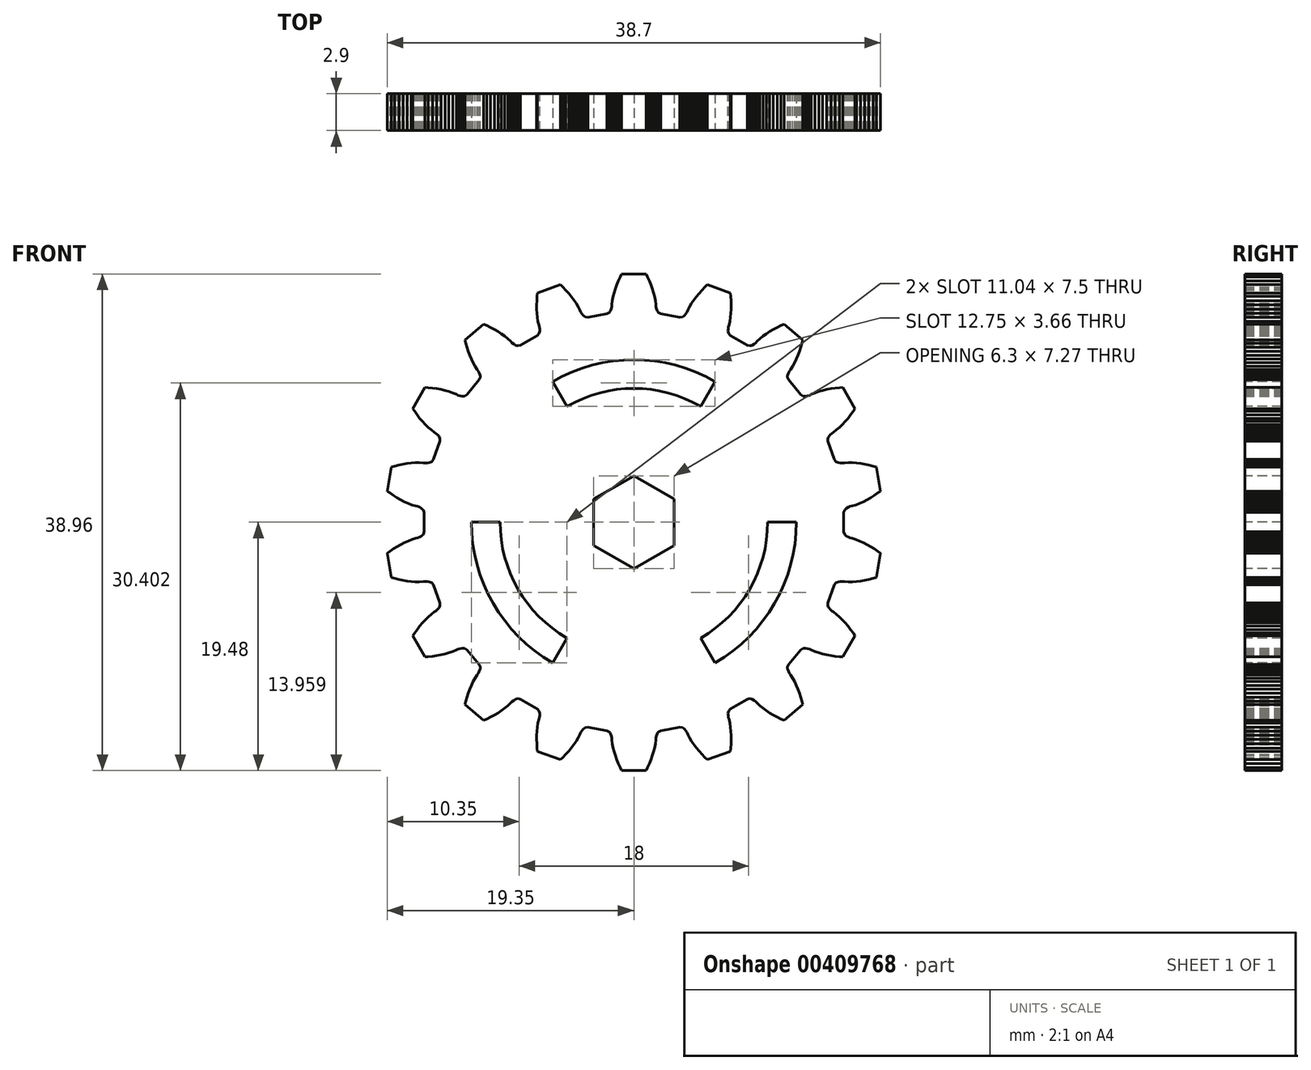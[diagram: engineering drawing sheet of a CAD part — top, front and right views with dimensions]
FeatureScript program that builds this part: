
annotation { "Feature Type Name" : "Feature", "Feature Type Description" : "" }
export const myFeature = defineFeature(function(context is Context, id is Id, definition is map)
    precondition{}
    {
        {
            var Q0;
            Q0=qCreatedBy(makeId("Front.planeOp"),FACE);
            var sketch = newSketch(context, id + "F0", { "sketchPlane" : qUnion([Q0])});
            skLineSegment(sketch, "E0", {"start": v(-16.48, 0.76) * mm, "end": v(-16.54, 0.96) * mm});
            skLineSegment(sketch, "E1", {"start": v(-16.54, 0.96) * mm, "end": v(-16.61, 1.04) * mm});
            skLineSegment(sketch, "E2", {"start": v(-16.61, 1.04) * mm, "end": v(-16.68, 1.1) * mm});
            skLineSegment(sketch, "E3", {"start": v(-16.68, 1.1) * mm, "end": v(-16.83, 1.17) * mm});
            skLineSegment(sketch, "E4", {"start": v(-16.83, 1.17) * mm, "end": v(-16.98, 1.24) * mm});
            skLineSegment(sketch, "E5", {"start": v(-16.98, 1.24) * mm, "end": v(-17.12, 1.27) * mm});
            skLineSegment(sketch, "E6", {"start": v(-17.12, 1.27) * mm, "end": v(-17.42, 1.36) * mm});
            skLineSegment(sketch, "E7", {"start": v(-17.42, 1.36) * mm, "end": v(-17.71, 1.47) * mm});
            skLineSegment(sketch, "E8", {"start": v(-17.71, 1.47) * mm, "end": v(-18, 1.6) * mm});
            skLineSegment(sketch, "E9", {"start": v(-18, 1.6) * mm, "end": v(-18.3, 1.75) * mm});
            skLineSegment(sketch, "E10", {"start": v(-18.3, 1.75) * mm, "end": v(-18.58, 1.92) * mm});
            skLineSegment(sketch, "E11", {"start": v(-18.58, 1.92) * mm, "end": v(-18.86, 2.1) * mm});
            skLineSegment(sketch, "E12", {"start": v(-18.86, 2.1) * mm, "end": v(-19.15, 2.29) * mm});
            skLineSegment(sketch, "E13", {"start": v(-19.15, 2.29) * mm, "end": v(-19.35, 2.44) * mm});
            skLineSegment(sketch, "E14", {"start": v(-19.35, 2.44) * mm, "end": v(-19.02, 4.33) * mm});
            skLineSegment(sketch, "E15", {"start": v(-19.02, 4.33) * mm, "end": v(-18.77, 4.4) * mm});
            skLineSegment(sketch, "E16", {"start": v(-18.77, 4.4) * mm, "end": v(-18.44, 4.48) * mm});
            skLineSegment(sketch, "E17", {"start": v(-18.44, 4.48) * mm, "end": v(-18.11, 4.56) * mm});
            skLineSegment(sketch, "E18", {"start": v(-18.11, 4.56) * mm, "end": v(-17.79, 4.61) * mm});
            skLineSegment(sketch, "E19", {"start": v(-17.79, 4.61) * mm, "end": v(-17.47, 4.65) * mm});
            skLineSegment(sketch, "E20", {"start": v(-17.47, 4.65) * mm, "end": v(-17.15, 4.67) * mm});
            skLineSegment(sketch, "E21", {"start": v(-17.15, 4.67) * mm, "end": v(-16.83, 4.68) * mm});
            skLineSegment(sketch, "E22", {"start": v(-16.83, 4.68) * mm, "end": v(-16.53, 4.66) * mm});
            skLineSegment(sketch, "E23", {"start": v(-16.53, 4.66) * mm, "end": v(-16.37, 4.64) * mm});
            skLineSegment(sketch, "E24", {"start": v(-16.37, 4.64) * mm, "end": v(-16.22, 4.65) * mm});
            skLineSegment(sketch, "E25", {"start": v(-16.22, 4.65) * mm, "end": v(-16.05, 4.68) * mm});
            skLineSegment(sketch, "E26", {"start": v(-16.05, 4.68) * mm, "end": v(-15.96, 4.7) * mm});
            skLineSegment(sketch, "E27", {"start": v(-15.96, 4.7) * mm, "end": v(-15.87, 4.76) * mm});
            skLineSegment(sketch, "E28", {"start": v(-15.87, 4.76) * mm, "end": v(-15.74, 4.92) * mm});
            skLineSegment(sketch, "E29", {"start": v(-15.74, 4.92) * mm, "end": v(-15.22, 6.35) * mm});
            skLineSegment(sketch, "E30", {"start": v(-15.22, 6.35) * mm, "end": v(-15.22, 6.56) * mm});
            skLineSegment(sketch, "E31", {"start": v(-15.22, 6.56) * mm, "end": v(-15.26, 6.65) * mm});
            skLineSegment(sketch, "E32", {"start": v(-15.26, 6.65) * mm, "end": v(-15.3, 6.73) * mm});
            skLineSegment(sketch, "E33", {"start": v(-15.3, 6.73) * mm, "end": v(-15.41, 6.86) * mm});
            skLineSegment(sketch, "E34", {"start": v(-15.41, 6.86) * mm, "end": v(-15.53, 6.97) * mm});
            skLineSegment(sketch, "E35", {"start": v(-15.53, 6.97) * mm, "end": v(-15.66, 7.05) * mm});
            skLineSegment(sketch, "E36", {"start": v(-15.66, 7.05) * mm, "end": v(-15.9, 7.24) * mm});
            skLineSegment(sketch, "E37", {"start": v(-15.9, 7.24) * mm, "end": v(-16.14, 7.44) * mm});
            skLineSegment(sketch, "E38", {"start": v(-16.14, 7.44) * mm, "end": v(-16.37, 7.66) * mm});
            skLineSegment(sketch, "E39", {"start": v(-16.37, 7.66) * mm, "end": v(-16.6, 7.9) * mm});
            skLineSegment(sketch, "E40", {"start": v(-16.6, 7.9) * mm, "end": v(-16.8, 8.15) * mm});
            skLineSegment(sketch, "E41", {"start": v(-16.8, 8.15) * mm, "end": v(-17.01, 8.42) * mm});
            skLineSegment(sketch, "E42", {"start": v(-17.01, 8.42) * mm, "end": v(-17.2, 8.7) * mm});
            skLineSegment(sketch, "E43", {"start": v(-17.2, 8.7) * mm, "end": v(-17.35, 8.91) * mm});
            skLineSegment(sketch, "E44", {"start": v(-17.35, 8.91) * mm, "end": v(-16.4, 10.57) * mm});
            skLineSegment(sketch, "E45", {"start": v(-16.4, 10.57) * mm, "end": v(-16.14, 10.55) * mm});
            skLineSegment(sketch, "E46", {"start": v(-16.14, 10.55) * mm, "end": v(-15.8, 10.52) * mm});
            skLineSegment(sketch, "E47", {"start": v(-15.8, 10.52) * mm, "end": v(-15.46, 10.48) * mm});
            skLineSegment(sketch, "E48", {"start": v(-15.46, 10.48) * mm, "end": v(-15.14, 10.42) * mm});
            skLineSegment(sketch, "E49", {"start": v(-15.14, 10.42) * mm, "end": v(-14.82, 10.34) * mm});
            skLineSegment(sketch, "E50", {"start": v(-14.82, 10.34) * mm, "end": v(-14.52, 10.26) * mm});
            skLineSegment(sketch, "E51", {"start": v(-14.52, 10.26) * mm, "end": v(-14.22, 10.16) * mm});
            skLineSegment(sketch, "E52", {"start": v(-14.22, 10.16) * mm, "end": v(-13.93, 10.03) * mm});
            skLineSegment(sketch, "E53", {"start": v(-13.93, 10.03) * mm, "end": v(-13.8, 9.96) * mm});
            skLineSegment(sketch, "E54", {"start": v(-13.8, 9.96) * mm, "end": v(-13.65, 9.92) * mm});
            skLineSegment(sketch, "E55", {"start": v(-13.65, 9.92) * mm, "end": v(-13.48, 9.89) * mm});
            skLineSegment(sketch, "E56", {"start": v(-13.48, 9.89) * mm, "end": v(-13.4, 9.88) * mm});
            skLineSegment(sketch, "E57", {"start": v(-13.4, 9.88) * mm, "end": v(-13.29, 9.9) * mm});
            skLineSegment(sketch, "E58", {"start": v(-13.29, 9.9) * mm, "end": v(-13.11, 10) * mm});
            skLineSegment(sketch, "E59", {"start": v(-13.11, 10) * mm, "end": v(-12.13, 11.17) * mm});
            skLineSegment(sketch, "E60", {"start": v(-12.13, 11.17) * mm, "end": v(-12.05, 11.37) * mm});
            skLineSegment(sketch, "E61", {"start": v(-12.05, 11.37) * mm, "end": v(-12.06, 11.47) * mm});
            skLineSegment(sketch, "E62", {"start": v(-12.06, 11.47) * mm, "end": v(-12.08, 11.56) * mm});
            skLineSegment(sketch, "E63", {"start": v(-12.08, 11.56) * mm, "end": v(-12.14, 11.72) * mm});
            skLineSegment(sketch, "E64", {"start": v(-12.14, 11.72) * mm, "end": v(-12.2, 11.86) * mm});
            skLineSegment(sketch, "E65", {"start": v(-12.2, 11.86) * mm, "end": v(-12.3, 11.98) * mm});
            skLineSegment(sketch, "E66", {"start": v(-12.3, 11.98) * mm, "end": v(-12.47, 12.24) * mm});
            skLineSegment(sketch, "E67", {"start": v(-12.47, 12.24) * mm, "end": v(-12.62, 12.51) * mm});
            skLineSegment(sketch, "E68", {"start": v(-12.62, 12.51) * mm, "end": v(-12.76, 12.8) * mm});
            skLineSegment(sketch, "E69", {"start": v(-12.76, 12.8) * mm, "end": v(-12.89, 13.1) * mm});
            skLineSegment(sketch, "E70", {"start": v(-12.89, 13.1) * mm, "end": v(-13, 13.41) * mm});
            skLineSegment(sketch, "E71", {"start": v(-13, 13.41) * mm, "end": v(-13.1, 13.73) * mm});
            skLineSegment(sketch, "E72", {"start": v(-13.1, 13.73) * mm, "end": v(-13.2, 14.06) * mm});
            skLineSegment(sketch, "E73", {"start": v(-13.2, 14.06) * mm, "end": v(-13.26, 14.3) * mm});
            skLineSegment(sketch, "E74", {"start": v(-13.26, 14.3) * mm, "end": v(-11.8, 15.54) * mm});
            skLineSegment(sketch, "E75", {"start": v(-11.8, 15.54) * mm, "end": v(-11.55, 15.44) * mm});
            skLineSegment(sketch, "E76", {"start": v(-11.55, 15.44) * mm, "end": v(-11.25, 15.29) * mm});
            skLineSegment(sketch, "E77", {"start": v(-11.25, 15.29) * mm, "end": v(-10.95, 15.13) * mm});
            skLineSegment(sketch, "E78", {"start": v(-10.95, 15.13) * mm, "end": v(-10.66, 14.97) * mm});
            skLineSegment(sketch, "E79", {"start": v(-10.66, 14.97) * mm, "end": v(-10.4, 14.8) * mm});
            skLineSegment(sketch, "E80", {"start": v(-10.4, 14.8) * mm, "end": v(-10.13, 14.6) * mm});
            skLineSegment(sketch, "E81", {"start": v(-10.13, 14.6) * mm, "end": v(-9.89, 14.4) * mm});
            skLineSegment(sketch, "E82", {"start": v(-9.89, 14.4) * mm, "end": v(-9.66, 14.2) * mm});
            skLineSegment(sketch, "E83", {"start": v(-9.66, 14.2) * mm, "end": v(-9.56, 14.08) * mm});
            skLineSegment(sketch, "E84", {"start": v(-9.56, 14.08) * mm, "end": v(-9.43, 13.99) * mm});
            skLineSegment(sketch, "E85", {"start": v(-9.43, 13.99) * mm, "end": v(-9.29, 13.9) * mm});
            skLineSegment(sketch, "E86", {"start": v(-9.29, 13.9) * mm, "end": v(-9.2, 13.87) * mm});
            skLineSegment(sketch, "E87", {"start": v(-9.2, 13.87) * mm, "end": v(-9.1, 13.85) * mm});
            skLineSegment(sketch, "E88", {"start": v(-9.1, 13.85) * mm, "end": v(-8.9, 13.89) * mm});
            skLineSegment(sketch, "E89", {"start": v(-8.9, 13.89) * mm, "end": v(-7.58, 14.65) * mm});
            skLineSegment(sketch, "E90", {"start": v(-7.58, 14.65) * mm, "end": v(-7.44, 14.8) * mm});
            skLineSegment(sketch, "E91", {"start": v(-7.44, 14.8) * mm, "end": v(-7.4, 14.9) * mm});
            skLineSegment(sketch, "E92", {"start": v(-7.4, 14.9) * mm, "end": v(-7.4, 15) * mm});
            skLineSegment(sketch, "E93", {"start": v(-7.4, 15) * mm, "end": v(-7.4, 15.16) * mm});
            skLineSegment(sketch, "E94", {"start": v(-7.4, 15.16) * mm, "end": v(-7.42, 15.32) * mm});
            skLineSegment(sketch, "E95", {"start": v(-7.42, 15.32) * mm, "end": v(-7.46, 15.47) * mm});
            skLineSegment(sketch, "E96", {"start": v(-7.46, 15.47) * mm, "end": v(-7.53, 15.77) * mm});
            skLineSegment(sketch, "E97", {"start": v(-7.53, 15.77) * mm, "end": v(-7.58, 16.08) * mm});
            skLineSegment(sketch, "E98", {"start": v(-7.58, 16.08) * mm, "end": v(-7.61, 16.4) * mm});
            skLineSegment(sketch, "E99", {"start": v(-7.61, 16.4) * mm, "end": v(-7.63, 16.72) * mm});
            skLineSegment(sketch, "E100", {"start": v(-7.63, 16.72) * mm, "end": v(-7.63, 17.05) * mm});
            skLineSegment(sketch, "E101", {"start": v(-7.63, 17.05) * mm, "end": v(-7.62, 17.38) * mm});
            skLineSegment(sketch, "E102", {"start": v(-7.62, 17.38) * mm, "end": v(-7.6, 17.72) * mm});
            skLineSegment(sketch, "E103", {"start": v(-7.6, 17.72) * mm, "end": v(-7.56, 17.98) * mm});
            skLineSegment(sketch, "E104", {"start": v(-7.56, 17.98) * mm, "end": v(-5.76, 18.64) * mm});
            skLineSegment(sketch, "E105", {"start": v(-5.76, 18.64) * mm, "end": v(-5.58, 18.46) * mm});
            skLineSegment(sketch, "E106", {"start": v(-5.58, 18.46) * mm, "end": v(-5.34, 18.21) * mm});
            skLineSegment(sketch, "E107", {"start": v(-5.34, 18.21) * mm, "end": v(-5.11, 17.97) * mm});
            skLineSegment(sketch, "E108", {"start": v(-5.11, 17.97) * mm, "end": v(-4.9, 17.71) * mm});
            skLineSegment(sketch, "E109", {"start": v(-4.9, 17.71) * mm, "end": v(-4.7, 17.45) * mm});
            skLineSegment(sketch, "E110", {"start": v(-4.7, 17.45) * mm, "end": v(-4.53, 17.19) * mm});
            skLineSegment(sketch, "E111", {"start": v(-4.53, 17.19) * mm, "end": v(-4.36, 16.92) * mm});
            skLineSegment(sketch, "E112", {"start": v(-4.36, 16.92) * mm, "end": v(-4.23, 16.64) * mm});
            skLineSegment(sketch, "E113", {"start": v(-4.23, 16.64) * mm, "end": v(-4.17, 16.5) * mm});
            skLineSegment(sketch, "E114", {"start": v(-4.17, 16.5) * mm, "end": v(-4.08, 16.37) * mm});
            skLineSegment(sketch, "E115", {"start": v(-4.08, 16.37) * mm, "end": v(-3.97, 16.24) * mm});
            skLineSegment(sketch, "E116", {"start": v(-3.97, 16.24) * mm, "end": v(-3.9, 16.18) * mm});
            skLineSegment(sketch, "E117", {"start": v(-3.9, 16.18) * mm, "end": v(-3.82, 16.12) * mm});
            skLineSegment(sketch, "E118", {"start": v(-3.82, 16.12) * mm, "end": v(-3.61, 16.1) * mm});
            skLineSegment(sketch, "E119", {"start": v(-3.61, 16.1) * mm, "end": v(-2.11, 16.36) * mm});
            skLineSegment(sketch, "E120", {"start": v(-2.11, 16.36) * mm, "end": v(-1.93, 16.46) * mm});
            skLineSegment(sketch, "E121", {"start": v(-1.93, 16.46) * mm, "end": v(-1.86, 16.54) * mm});
            skLineSegment(sketch, "E122", {"start": v(-1.86, 16.54) * mm, "end": v(-1.82, 16.62) * mm});
            skLineSegment(sketch, "E123", {"start": v(-1.82, 16.62) * mm, "end": v(-1.77, 16.78) * mm});
            skLineSegment(sketch, "E124", {"start": v(-1.77, 16.78) * mm, "end": v(-1.73, 16.93) * mm});
            skLineSegment(sketch, "E125", {"start": v(-1.73, 16.93) * mm, "end": v(-1.72, 17.08) * mm});
            skLineSegment(sketch, "E126", {"start": v(-1.72, 17.08) * mm, "end": v(-1.69, 17.4) * mm});
            skLineSegment(sketch, "E127", {"start": v(-1.69, 17.4) * mm, "end": v(-1.63, 17.7) * mm});
            skLineSegment(sketch, "E128", {"start": v(-1.63, 17.7) * mm, "end": v(-1.55, 18) * mm});
            skLineSegment(sketch, "E129", {"start": v(-1.55, 18) * mm, "end": v(-1.45, 18.32) * mm});
            skLineSegment(sketch, "E130", {"start": v(-1.45, 18.32) * mm, "end": v(-1.34, 18.63) * mm});
            skLineSegment(sketch, "E131", {"start": v(-1.34, 18.63) * mm, "end": v(-1.21, 18.94) * mm});
            skLineSegment(sketch, "E132", {"start": v(-1.21, 18.94) * mm, "end": v(-1.07, 19.25) * mm});
            skLineSegment(sketch, "E133", {"start": v(-1.07, 19.25) * mm, "end": v(-0.96, 19.48) * mm});
            skLineSegment(sketch, "E134", {"start": v(-0.96, 19.48) * mm, "end": v(0.96, 19.48) * mm});
            skLineSegment(sketch, "E135", {"start": v(0.96, 19.48) * mm, "end": v(1.07, 19.25) * mm});
            skLineSegment(sketch, "E136", {"start": v(1.07, 19.25) * mm, "end": v(1.21, 18.94) * mm});
            skLineSegment(sketch, "E137", {"start": v(1.21, 18.94) * mm, "end": v(1.34, 18.63) * mm});
            skLineSegment(sketch, "E138", {"start": v(1.34, 18.63) * mm, "end": v(1.45, 18.32) * mm});
            skLineSegment(sketch, "E139", {"start": v(1.45, 18.32) * mm, "end": v(1.55, 18) * mm});
            skLineSegment(sketch, "E140", {"start": v(1.55, 18) * mm, "end": v(1.63, 17.7) * mm});
            skLineSegment(sketch, "E141", {"start": v(1.63, 17.7) * mm, "end": v(1.69, 17.4) * mm});
            skLineSegment(sketch, "E142", {"start": v(1.69, 17.4) * mm, "end": v(1.72, 17.08) * mm});
            skLineSegment(sketch, "E143", {"start": v(1.72, 17.08) * mm, "end": v(1.73, 16.93) * mm});
            skLineSegment(sketch, "E144", {"start": v(1.73, 16.93) * mm, "end": v(1.77, 16.78) * mm});
            skLineSegment(sketch, "E145", {"start": v(1.77, 16.78) * mm, "end": v(1.82, 16.62) * mm});
            skLineSegment(sketch, "E146", {"start": v(1.82, 16.62) * mm, "end": v(1.86, 16.54) * mm});
            skLineSegment(sketch, "E147", {"start": v(1.86, 16.54) * mm, "end": v(1.93, 16.46) * mm});
            skLineSegment(sketch, "E148", {"start": v(1.93, 16.46) * mm, "end": v(2.11, 16.36) * mm});
            skLineSegment(sketch, "E149", {"start": v(2.11, 16.36) * mm, "end": v(3.61, 16.1) * mm});
            skLineSegment(sketch, "E150", {"start": v(3.61, 16.1) * mm, "end": v(3.82, 16.12) * mm});
            skLineSegment(sketch, "E151", {"start": v(3.82, 16.12) * mm, "end": v(3.9, 16.18) * mm});
            skLineSegment(sketch, "E152", {"start": v(3.9, 16.18) * mm, "end": v(3.97, 16.24) * mm});
            skLineSegment(sketch, "E153", {"start": v(3.97, 16.24) * mm, "end": v(4.08, 16.37) * mm});
            skLineSegment(sketch, "E154", {"start": v(4.08, 16.37) * mm, "end": v(4.17, 16.5) * mm});
            skLineSegment(sketch, "E155", {"start": v(4.17, 16.5) * mm, "end": v(4.23, 16.64) * mm});
            skLineSegment(sketch, "E156", {"start": v(4.23, 16.64) * mm, "end": v(4.36, 16.92) * mm});
            skLineSegment(sketch, "E157", {"start": v(4.36, 16.92) * mm, "end": v(4.53, 17.19) * mm});
            skLineSegment(sketch, "E158", {"start": v(4.53, 17.19) * mm, "end": v(4.7, 17.45) * mm});
            skLineSegment(sketch, "E159", {"start": v(4.7, 17.45) * mm, "end": v(4.9, 17.71) * mm});
            skLineSegment(sketch, "E160", {"start": v(4.9, 17.71) * mm, "end": v(5.11, 17.97) * mm});
            skLineSegment(sketch, "E161", {"start": v(5.11, 17.97) * mm, "end": v(5.34, 18.21) * mm});
            skLineSegment(sketch, "E162", {"start": v(5.34, 18.21) * mm, "end": v(5.58, 18.46) * mm});
            skLineSegment(sketch, "E163", {"start": v(5.58, 18.46) * mm, "end": v(5.76, 18.64) * mm});
            skLineSegment(sketch, "E164", {"start": v(5.76, 18.64) * mm, "end": v(7.56, 17.98) * mm});
            skLineSegment(sketch, "E165", {"start": v(7.56, 17.98) * mm, "end": v(7.6, 17.72) * mm});
            skLineSegment(sketch, "E166", {"start": v(7.6, 17.72) * mm, "end": v(7.62, 17.38) * mm});
            skLineSegment(sketch, "E167", {"start": v(7.62, 17.38) * mm, "end": v(7.63, 17.05) * mm});
            skLineSegment(sketch, "E168", {"start": v(7.63, 17.05) * mm, "end": v(7.63, 16.72) * mm});
            skLineSegment(sketch, "E169", {"start": v(7.63, 16.72) * mm, "end": v(7.61, 16.4) * mm});
            skLineSegment(sketch, "E170", {"start": v(7.61, 16.4) * mm, "end": v(7.58, 16.08) * mm});
            skLineSegment(sketch, "E171", {"start": v(7.58, 16.08) * mm, "end": v(7.53, 15.77) * mm});
            skLineSegment(sketch, "E172", {"start": v(7.53, 15.77) * mm, "end": v(7.46, 15.47) * mm});
            skLineSegment(sketch, "E173", {"start": v(7.46, 15.47) * mm, "end": v(7.42, 15.32) * mm});
            skLineSegment(sketch, "E174", {"start": v(7.42, 15.32) * mm, "end": v(7.4, 15.16) * mm});
            skLineSegment(sketch, "E175", {"start": v(7.4, 15.16) * mm, "end": v(7.4, 15) * mm});
            skLineSegment(sketch, "E176", {"start": v(7.4, 15) * mm, "end": v(7.4, 14.9) * mm});
            skLineSegment(sketch, "E177", {"start": v(7.4, 14.9) * mm, "end": v(7.44, 14.8) * mm});
            skLineSegment(sketch, "E178", {"start": v(7.44, 14.8) * mm, "end": v(7.58, 14.65) * mm});
            skLineSegment(sketch, "E179", {"start": v(7.58, 14.65) * mm, "end": v(8.9, 13.89) * mm});
            skLineSegment(sketch, "E180", {"start": v(8.9, 13.89) * mm, "end": v(9.1, 13.85) * mm});
            skLineSegment(sketch, "E181", {"start": v(9.1, 13.85) * mm, "end": v(9.2, 13.87) * mm});
            skLineSegment(sketch, "E182", {"start": v(9.2, 13.87) * mm, "end": v(9.29, 13.9) * mm});
            skLineSegment(sketch, "E183", {"start": v(9.29, 13.9) * mm, "end": v(9.43, 13.99) * mm});
            skLineSegment(sketch, "E184", {"start": v(9.43, 13.99) * mm, "end": v(9.56, 14.08) * mm});
            skLineSegment(sketch, "E185", {"start": v(9.56, 14.08) * mm, "end": v(9.66, 14.2) * mm});
            skLineSegment(sketch, "E186", {"start": v(9.66, 14.2) * mm, "end": v(9.89, 14.4) * mm});
            skLineSegment(sketch, "E187", {"start": v(9.89, 14.4) * mm, "end": v(10.13, 14.6) * mm});
            skLineSegment(sketch, "E188", {"start": v(10.13, 14.6) * mm, "end": v(10.4, 14.8) * mm});
            skLineSegment(sketch, "E189", {"start": v(10.4, 14.8) * mm, "end": v(10.66, 14.97) * mm});
            skLineSegment(sketch, "E190", {"start": v(10.66, 14.97) * mm, "end": v(10.95, 15.13) * mm});
            skLineSegment(sketch, "E191", {"start": v(10.95, 15.13) * mm, "end": v(11.25, 15.29) * mm});
            skLineSegment(sketch, "E192", {"start": v(11.25, 15.29) * mm, "end": v(11.55, 15.44) * mm});
            skLineSegment(sketch, "E193", {"start": v(11.55, 15.44) * mm, "end": v(11.8, 15.54) * mm});
            skLineSegment(sketch, "E194", {"start": v(11.8, 15.54) * mm, "end": v(13.26, 14.3) * mm});
            skLineSegment(sketch, "E195", {"start": v(13.26, 14.3) * mm, "end": v(13.2, 14.06) * mm});
            skLineSegment(sketch, "E196", {"start": v(13.2, 14.06) * mm, "end": v(13.1, 13.73) * mm});
            skLineSegment(sketch, "E197", {"start": v(13.1, 13.73) * mm, "end": v(13, 13.41) * mm});
            skLineSegment(sketch, "E198", {"start": v(13, 13.41) * mm, "end": v(12.89, 13.1) * mm});
            skLineSegment(sketch, "E199", {"start": v(12.89, 13.1) * mm, "end": v(12.76, 12.8) * mm});
            skLineSegment(sketch, "E200", {"start": v(12.76, 12.8) * mm, "end": v(12.62, 12.51) * mm});
            skLineSegment(sketch, "E201", {"start": v(12.62, 12.51) * mm, "end": v(12.47, 12.24) * mm});
            skLineSegment(sketch, "E202", {"start": v(12.47, 12.24) * mm, "end": v(12.3, 11.98) * mm});
            skLineSegment(sketch, "E203", {"start": v(12.3, 11.98) * mm, "end": v(12.2, 11.86) * mm});
            skLineSegment(sketch, "E204", {"start": v(12.2, 11.86) * mm, "end": v(12.14, 11.72) * mm});
            skLineSegment(sketch, "E205", {"start": v(12.14, 11.72) * mm, "end": v(12.08, 11.56) * mm});
            skLineSegment(sketch, "E206", {"start": v(12.08, 11.56) * mm, "end": v(12.06, 11.47) * mm});
            skLineSegment(sketch, "E207", {"start": v(12.06, 11.47) * mm, "end": v(12.05, 11.37) * mm});
            skLineSegment(sketch, "E208", {"start": v(12.05, 11.37) * mm, "end": v(12.13, 11.17) * mm});
            skLineSegment(sketch, "E209", {"start": v(12.13, 11.17) * mm, "end": v(13.11, 10) * mm});
            skLineSegment(sketch, "E210", {"start": v(13.11, 10) * mm, "end": v(13.29, 9.9) * mm});
            skLineSegment(sketch, "E211", {"start": v(13.29, 9.9) * mm, "end": v(13.4, 9.88) * mm});
            skLineSegment(sketch, "E212", {"start": v(13.4, 9.88) * mm, "end": v(13.48, 9.89) * mm});
            skLineSegment(sketch, "E213", {"start": v(13.48, 9.89) * mm, "end": v(13.65, 9.92) * mm});
            skLineSegment(sketch, "E214", {"start": v(13.65, 9.92) * mm, "end": v(13.8, 9.96) * mm});
            skLineSegment(sketch, "E215", {"start": v(13.8, 9.96) * mm, "end": v(13.93, 10.03) * mm});
            skLineSegment(sketch, "E216", {"start": v(13.93, 10.03) * mm, "end": v(14.22, 10.16) * mm});
            skLineSegment(sketch, "E217", {"start": v(14.22, 10.16) * mm, "end": v(14.52, 10.26) * mm});
            skLineSegment(sketch, "E218", {"start": v(14.52, 10.26) * mm, "end": v(14.82, 10.34) * mm});
            skLineSegment(sketch, "E219", {"start": v(14.82, 10.34) * mm, "end": v(15.14, 10.42) * mm});
            skLineSegment(sketch, "E220", {"start": v(15.14, 10.42) * mm, "end": v(15.46, 10.48) * mm});
            skLineSegment(sketch, "E221", {"start": v(15.46, 10.48) * mm, "end": v(15.8, 10.52) * mm});
            skLineSegment(sketch, "E222", {"start": v(15.8, 10.52) * mm, "end": v(16.14, 10.55) * mm});
            skLineSegment(sketch, "E223", {"start": v(16.14, 10.55) * mm, "end": v(16.4, 10.57) * mm});
            skLineSegment(sketch, "E224", {"start": v(16.4, 10.57) * mm, "end": v(17.35, 8.91) * mm});
            skLineSegment(sketch, "E225", {"start": v(17.35, 8.91) * mm, "end": v(17.2, 8.7) * mm});
            skLineSegment(sketch, "E226", {"start": v(17.2, 8.7) * mm, "end": v(17.01, 8.42) * mm});
            skLineSegment(sketch, "E227", {"start": v(17.01, 8.42) * mm, "end": v(16.8, 8.15) * mm});
            skLineSegment(sketch, "E228", {"start": v(16.8, 8.15) * mm, "end": v(16.6, 7.9) * mm});
            skLineSegment(sketch, "E229", {"start": v(16.6, 7.9) * mm, "end": v(16.37, 7.66) * mm});
            skLineSegment(sketch, "E230", {"start": v(16.37, 7.66) * mm, "end": v(16.14, 7.44) * mm});
            skLineSegment(sketch, "E231", {"start": v(16.14, 7.44) * mm, "end": v(15.9, 7.24) * mm});
            skLineSegment(sketch, "E232", {"start": v(15.9, 7.24) * mm, "end": v(15.66, 7.05) * mm});
            skLineSegment(sketch, "E233", {"start": v(15.66, 7.05) * mm, "end": v(15.53, 6.97) * mm});
            skLineSegment(sketch, "E234", {"start": v(15.53, 6.97) * mm, "end": v(15.41, 6.86) * mm});
            skLineSegment(sketch, "E235", {"start": v(15.41, 6.86) * mm, "end": v(15.3, 6.73) * mm});
            skLineSegment(sketch, "E236", {"start": v(15.3, 6.73) * mm, "end": v(15.26, 6.65) * mm});
            skLineSegment(sketch, "E237", {"start": v(15.26, 6.65) * mm, "end": v(15.22, 6.56) * mm});
            skLineSegment(sketch, "E238", {"start": v(15.22, 6.56) * mm, "end": v(15.22, 6.35) * mm});
            skLineSegment(sketch, "E239", {"start": v(15.22, 6.35) * mm, "end": v(15.74, 4.92) * mm});
            skLineSegment(sketch, "E240", {"start": v(15.74, 4.92) * mm, "end": v(15.87, 4.76) * mm});
            skLineSegment(sketch, "E241", {"start": v(15.87, 4.76) * mm, "end": v(15.96, 4.7) * mm});
            skLineSegment(sketch, "E242", {"start": v(15.96, 4.7) * mm, "end": v(16.05, 4.68) * mm});
            skLineSegment(sketch, "E243", {"start": v(16.05, 4.68) * mm, "end": v(16.22, 4.65) * mm});
            skLineSegment(sketch, "E244", {"start": v(16.22, 4.65) * mm, "end": v(16.37, 4.64) * mm});
            skLineSegment(sketch, "E245", {"start": v(16.37, 4.64) * mm, "end": v(16.53, 4.66) * mm});
            skLineSegment(sketch, "E246", {"start": v(16.53, 4.66) * mm, "end": v(16.83, 4.68) * mm});
            skLineSegment(sketch, "E247", {"start": v(16.83, 4.68) * mm, "end": v(17.15, 4.67) * mm});
            skLineSegment(sketch, "E248", {"start": v(17.15, 4.67) * mm, "end": v(17.47, 4.65) * mm});
            skLineSegment(sketch, "E249", {"start": v(17.47, 4.65) * mm, "end": v(17.79, 4.61) * mm});
            skLineSegment(sketch, "E250", {"start": v(17.79, 4.61) * mm, "end": v(18.11, 4.56) * mm});
            skLineSegment(sketch, "E251", {"start": v(18.11, 4.56) * mm, "end": v(18.44, 4.48) * mm});
            skLineSegment(sketch, "E252", {"start": v(18.44, 4.48) * mm, "end": v(18.77, 4.4) * mm});
            skLineSegment(sketch, "E253", {"start": v(18.77, 4.4) * mm, "end": v(19.02, 4.33) * mm});
            skLineSegment(sketch, "E254", {"start": v(19.02, 4.33) * mm, "end": v(19.35, 2.44) * mm});
            skLineSegment(sketch, "E255", {"start": v(19.35, 2.44) * mm, "end": v(19.15, 2.29) * mm});
            skLineSegment(sketch, "E256", {"start": v(19.15, 2.29) * mm, "end": v(18.86, 2.1) * mm});
            skLineSegment(sketch, "E257", {"start": v(18.86, 2.1) * mm, "end": v(18.58, 1.92) * mm});
            skLineSegment(sketch, "E258", {"start": v(18.58, 1.92) * mm, "end": v(18.3, 1.75) * mm});
            skLineSegment(sketch, "E259", {"start": v(18.3, 1.75) * mm, "end": v(18, 1.6) * mm});
            skLineSegment(sketch, "E260", {"start": v(18, 1.6) * mm, "end": v(17.71, 1.47) * mm});
            skLineSegment(sketch, "E261", {"start": v(17.71, 1.47) * mm, "end": v(17.42, 1.36) * mm});
            skLineSegment(sketch, "E262", {"start": v(17.42, 1.36) * mm, "end": v(17.12, 1.27) * mm});
            skLineSegment(sketch, "E263", {"start": v(17.12, 1.27) * mm, "end": v(16.98, 1.24) * mm});
            skLineSegment(sketch, "E264", {"start": v(16.98, 1.24) * mm, "end": v(16.83, 1.17) * mm});
            skLineSegment(sketch, "E265", {"start": v(16.83, 1.17) * mm, "end": v(16.68, 1.1) * mm});
            skLineSegment(sketch, "E266", {"start": v(16.68, 1.1) * mm, "end": v(16.61, 1.04) * mm});
            skLineSegment(sketch, "E267", {"start": v(16.61, 1.04) * mm, "end": v(16.54, 0.96) * mm});
            skLineSegment(sketch, "E268", {"start": v(16.54, 0.96) * mm, "end": v(16.48, 0.76) * mm});
            skLineSegment(sketch, "E269", {"start": v(16.48, 0.76) * mm, "end": v(16.48, -0.76) * mm});
            skLineSegment(sketch, "E270", {"start": v(16.48, -0.76) * mm, "end": v(16.54, -0.96) * mm});
            skLineSegment(sketch, "E271", {"start": v(16.54, -0.96) * mm, "end": v(16.61, -1.04) * mm});
            skLineSegment(sketch, "E272", {"start": v(16.61, -1.04) * mm, "end": v(16.68, -1.1) * mm});
            skLineSegment(sketch, "E273", {"start": v(16.68, -1.1) * mm, "end": v(16.83, -1.17) * mm});
            skLineSegment(sketch, "E274", {"start": v(16.83, -1.17) * mm, "end": v(16.98, -1.24) * mm});
            skLineSegment(sketch, "E275", {"start": v(16.98, -1.24) * mm, "end": v(17.12, -1.27) * mm});
            skLineSegment(sketch, "E276", {"start": v(17.12, -1.27) * mm, "end": v(17.42, -1.36) * mm});
            skLineSegment(sketch, "E277", {"start": v(17.42, -1.36) * mm, "end": v(17.71, -1.47) * mm});
            skLineSegment(sketch, "E278", {"start": v(17.71, -1.47) * mm, "end": v(18, -1.6) * mm});
            skLineSegment(sketch, "E279", {"start": v(18, -1.6) * mm, "end": v(18.3, -1.75) * mm});
            skLineSegment(sketch, "E280", {"start": v(18.3, -1.75) * mm, "end": v(18.58, -1.92) * mm});
            skLineSegment(sketch, "E281", {"start": v(18.58, -1.92) * mm, "end": v(18.86, -2.1) * mm});
            skLineSegment(sketch, "E282", {"start": v(18.86, -2.1) * mm, "end": v(19.15, -2.29) * mm});
            skLineSegment(sketch, "E283", {"start": v(19.15, -2.29) * mm, "end": v(19.35, -2.44) * mm});
            skLineSegment(sketch, "E284", {"start": v(19.35, -2.44) * mm, "end": v(19.02, -4.33) * mm});
            skLineSegment(sketch, "E285", {"start": v(19.02, -4.33) * mm, "end": v(18.77, -4.4) * mm});
            skLineSegment(sketch, "E286", {"start": v(18.77, -4.4) * mm, "end": v(18.44, -4.48) * mm});
            skLineSegment(sketch, "E287", {"start": v(18.44, -4.48) * mm, "end": v(18.11, -4.55) * mm});
            skLineSegment(sketch, "E288", {"start": v(18.11, -4.55) * mm, "end": v(17.79, -4.61) * mm});
            skLineSegment(sketch, "E289", {"start": v(17.79, -4.61) * mm, "end": v(17.47, -4.65) * mm});
            skLineSegment(sketch, "E290", {"start": v(17.47, -4.65) * mm, "end": v(17.15, -4.67) * mm});
            skLineSegment(sketch, "E291", {"start": v(17.15, -4.67) * mm, "end": v(16.83, -4.68) * mm});
            skLineSegment(sketch, "E292", {"start": v(16.83, -4.68) * mm, "end": v(16.53, -4.66) * mm});
            skLineSegment(sketch, "E293", {"start": v(16.53, -4.66) * mm, "end": v(16.37, -4.64) * mm});
            skLineSegment(sketch, "E294", {"start": v(16.37, -4.64) * mm, "end": v(16.22, -4.65) * mm});
            skLineSegment(sketch, "E295", {"start": v(16.22, -4.65) * mm, "end": v(16.05, -4.68) * mm});
            skLineSegment(sketch, "E296", {"start": v(16.05, -4.68) * mm, "end": v(15.96, -4.7) * mm});
            skLineSegment(sketch, "E297", {"start": v(15.96, -4.7) * mm, "end": v(15.87, -4.76) * mm});
            skLineSegment(sketch, "E298", {"start": v(15.87, -4.76) * mm, "end": v(15.74, -4.92) * mm});
            skLineSegment(sketch, "E299", {"start": v(15.74, -4.92) * mm, "end": v(15.22, -6.35) * mm});
            skLineSegment(sketch, "E300", {"start": v(15.22, -6.35) * mm, "end": v(15.22, -6.56) * mm});
            skLineSegment(sketch, "E301", {"start": v(15.22, -6.56) * mm, "end": v(15.26, -6.65) * mm});
            skLineSegment(sketch, "E302", {"start": v(15.26, -6.65) * mm, "end": v(15.3, -6.73) * mm});
            skLineSegment(sketch, "E303", {"start": v(15.3, -6.73) * mm, "end": v(15.41, -6.86) * mm});
            skLineSegment(sketch, "E304", {"start": v(15.41, -6.86) * mm, "end": v(15.53, -6.97) * mm});
            skLineSegment(sketch, "E305", {"start": v(15.53, -6.97) * mm, "end": v(15.66, -7.05) * mm});
            skLineSegment(sketch, "E306", {"start": v(15.66, -7.05) * mm, "end": v(15.9, -7.24) * mm});
            skLineSegment(sketch, "E307", {"start": v(15.9, -7.24) * mm, "end": v(16.14, -7.44) * mm});
            skLineSegment(sketch, "E308", {"start": v(16.14, -7.44) * mm, "end": v(16.37, -7.66) * mm});
            skLineSegment(sketch, "E309", {"start": v(16.37, -7.66) * mm, "end": v(16.6, -7.9) * mm});
            skLineSegment(sketch, "E310", {"start": v(16.6, -7.9) * mm, "end": v(16.8, -8.15) * mm});
            skLineSegment(sketch, "E311", {"start": v(16.8, -8.15) * mm, "end": v(17.01, -8.42) * mm});
            skLineSegment(sketch, "E312", {"start": v(17.01, -8.42) * mm, "end": v(17.2, -8.7) * mm});
            skLineSegment(sketch, "E313", {"start": v(17.2, -8.7) * mm, "end": v(17.35, -8.91) * mm});
            skLineSegment(sketch, "E314", {"start": v(17.35, -8.91) * mm, "end": v(16.4, -10.57) * mm});
            skLineSegment(sketch, "E315", {"start": v(16.4, -10.57) * mm, "end": v(16.14, -10.55) * mm});
            skLineSegment(sketch, "E316", {"start": v(16.14, -10.55) * mm, "end": v(15.8, -10.52) * mm});
            skLineSegment(sketch, "E317", {"start": v(15.8, -10.52) * mm, "end": v(15.46, -10.48) * mm});
            skLineSegment(sketch, "E318", {"start": v(15.46, -10.48) * mm, "end": v(15.14, -10.42) * mm});
            skLineSegment(sketch, "E319", {"start": v(15.14, -10.42) * mm, "end": v(14.82, -10.34) * mm});
            skLineSegment(sketch, "E320", {"start": v(14.82, -10.34) * mm, "end": v(14.52, -10.26) * mm});
            skLineSegment(sketch, "E321", {"start": v(14.52, -10.26) * mm, "end": v(14.22, -10.15) * mm});
            skLineSegment(sketch, "E322", {"start": v(14.22, -10.15) * mm, "end": v(13.93, -10.03) * mm});
            skLineSegment(sketch, "E323", {"start": v(13.93, -10.03) * mm, "end": v(13.8, -9.96) * mm});
            skLineSegment(sketch, "E324", {"start": v(13.8, -9.96) * mm, "end": v(13.65, -9.92) * mm});
            skLineSegment(sketch, "E325", {"start": v(13.65, -9.92) * mm, "end": v(13.48, -9.89) * mm});
            skLineSegment(sketch, "E326", {"start": v(13.48, -9.89) * mm, "end": v(13.4, -9.88) * mm});
            skLineSegment(sketch, "E327", {"start": v(13.4, -9.88) * mm, "end": v(13.29, -9.9) * mm});
            skLineSegment(sketch, "E328", {"start": v(13.29, -9.9) * mm, "end": v(13.11, -10) * mm});
            skLineSegment(sketch, "E329", {"start": v(13.11, -10) * mm, "end": v(12.13, -11.17) * mm});
            skLineSegment(sketch, "E330", {"start": v(12.13, -11.17) * mm, "end": v(12.05, -11.37) * mm});
            skLineSegment(sketch, "E331", {"start": v(12.05, -11.37) * mm, "end": v(12.06, -11.47) * mm});
            skLineSegment(sketch, "E332", {"start": v(12.06, -11.47) * mm, "end": v(12.08, -11.56) * mm});
            skLineSegment(sketch, "E333", {"start": v(12.08, -11.56) * mm, "end": v(12.14, -11.72) * mm});
            skLineSegment(sketch, "E334", {"start": v(12.14, -11.72) * mm, "end": v(12.2, -11.86) * mm});
            skLineSegment(sketch, "E335", {"start": v(12.2, -11.86) * mm, "end": v(12.3, -11.98) * mm});
            skLineSegment(sketch, "E336", {"start": v(12.3, -11.98) * mm, "end": v(12.47, -12.24) * mm});
            skLineSegment(sketch, "E337", {"start": v(12.47, -12.24) * mm, "end": v(12.62, -12.51) * mm});
            skLineSegment(sketch, "E338", {"start": v(12.62, -12.51) * mm, "end": v(12.76, -12.8) * mm});
            skLineSegment(sketch, "E339", {"start": v(12.76, -12.8) * mm, "end": v(12.89, -13.1) * mm});
            skLineSegment(sketch, "E340", {"start": v(12.89, -13.1) * mm, "end": v(13, -13.4) * mm});
            skLineSegment(sketch, "E341", {"start": v(13, -13.4) * mm, "end": v(13.1, -13.73) * mm});
            skLineSegment(sketch, "E342", {"start": v(13.1, -13.73) * mm, "end": v(13.2, -14.06) * mm});
            skLineSegment(sketch, "E343", {"start": v(13.2, -14.06) * mm, "end": v(13.26, -14.3) * mm});
            skLineSegment(sketch, "E344", {"start": v(13.26, -14.3) * mm, "end": v(11.8, -15.54) * mm});
            skLineSegment(sketch, "E345", {"start": v(11.8, -15.54) * mm, "end": v(11.55, -15.44) * mm});
            skLineSegment(sketch, "E346", {"start": v(11.55, -15.44) * mm, "end": v(11.25, -15.29) * mm});
            skLineSegment(sketch, "E347", {"start": v(11.25, -15.29) * mm, "end": v(10.95, -15.13) * mm});
            skLineSegment(sketch, "E348", {"start": v(10.95, -15.13) * mm, "end": v(10.66, -14.97) * mm});
            skLineSegment(sketch, "E349", {"start": v(10.66, -14.97) * mm, "end": v(10.4, -14.8) * mm});
            skLineSegment(sketch, "E350", {"start": v(10.4, -14.8) * mm, "end": v(10.13, -14.6) * mm});
            skLineSegment(sketch, "E351", {"start": v(10.13, -14.6) * mm, "end": v(9.89, -14.4) * mm});
            skLineSegment(sketch, "E352", {"start": v(9.89, -14.4) * mm, "end": v(9.66, -14.2) * mm});
            skLineSegment(sketch, "E353", {"start": v(9.66, -14.2) * mm, "end": v(9.56, -14.08) * mm});
            skLineSegment(sketch, "E354", {"start": v(9.56, -14.08) * mm, "end": v(9.43, -13.99) * mm});
            skLineSegment(sketch, "E355", {"start": v(9.43, -13.99) * mm, "end": v(9.29, -13.9) * mm});
            skLineSegment(sketch, "E356", {"start": v(9.29, -13.9) * mm, "end": v(9.2, -13.87) * mm});
            skLineSegment(sketch, "E357", {"start": v(9.2, -13.87) * mm, "end": v(9.1, -13.85) * mm});
            skLineSegment(sketch, "E358", {"start": v(9.1, -13.85) * mm, "end": v(8.9, -13.89) * mm});
            skLineSegment(sketch, "E359", {"start": v(8.9, -13.89) * mm, "end": v(7.58, -14.65) * mm});
            skLineSegment(sketch, "E360", {"start": v(7.58, -14.65) * mm, "end": v(7.44, -14.8) * mm});
            skLineSegment(sketch, "E361", {"start": v(7.44, -14.8) * mm, "end": v(7.4, -14.9) * mm});
            skLineSegment(sketch, "E362", {"start": v(7.4, -14.9) * mm, "end": v(7.4, -15) * mm});
            skLineSegment(sketch, "E363", {"start": v(7.4, -15) * mm, "end": v(7.4, -15.16) * mm});
            skLineSegment(sketch, "E364", {"start": v(7.4, -15.16) * mm, "end": v(7.42, -15.32) * mm});
            skLineSegment(sketch, "E365", {"start": v(7.42, -15.32) * mm, "end": v(7.46, -15.47) * mm});
            skLineSegment(sketch, "E366", {"start": v(7.46, -15.47) * mm, "end": v(7.53, -15.77) * mm});
            skLineSegment(sketch, "E367", {"start": v(7.53, -15.77) * mm, "end": v(7.58, -16.08) * mm});
            skLineSegment(sketch, "E368", {"start": v(7.58, -16.08) * mm, "end": v(7.61, -16.4) * mm});
            skLineSegment(sketch, "E369", {"start": v(7.61, -16.4) * mm, "end": v(7.63, -16.72) * mm});
            skLineSegment(sketch, "E370", {"start": v(7.63, -16.72) * mm, "end": v(7.63, -17.05) * mm});
            skLineSegment(sketch, "E371", {"start": v(7.63, -17.05) * mm, "end": v(7.62, -17.38) * mm});
            skLineSegment(sketch, "E372", {"start": v(7.62, -17.38) * mm, "end": v(7.6, -17.72) * mm});
            skLineSegment(sketch, "E373", {"start": v(7.6, -17.72) * mm, "end": v(7.56, -17.98) * mm});
            skLineSegment(sketch, "E374", {"start": v(7.56, -17.98) * mm, "end": v(5.76, -18.64) * mm});
            skLineSegment(sketch, "E375", {"start": v(5.76, -18.64) * mm, "end": v(5.58, -18.46) * mm});
            skLineSegment(sketch, "E376", {"start": v(5.58, -18.46) * mm, "end": v(5.34, -18.21) * mm});
            skLineSegment(sketch, "E377", {"start": v(5.34, -18.21) * mm, "end": v(5.11, -17.96) * mm});
            skLineSegment(sketch, "E378", {"start": v(5.11, -17.96) * mm, "end": v(4.9, -17.71) * mm});
            skLineSegment(sketch, "E379", {"start": v(4.9, -17.71) * mm, "end": v(4.7, -17.45) * mm});
            skLineSegment(sketch, "E380", {"start": v(4.7, -17.45) * mm, "end": v(4.53, -17.19) * mm});
            skLineSegment(sketch, "E381", {"start": v(4.53, -17.19) * mm, "end": v(4.36, -16.92) * mm});
            skLineSegment(sketch, "E382", {"start": v(4.36, -16.92) * mm, "end": v(4.23, -16.64) * mm});
            skLineSegment(sketch, "E383", {"start": v(4.23, -16.64) * mm, "end": v(4.17, -16.5) * mm});
            skLineSegment(sketch, "E384", {"start": v(4.17, -16.5) * mm, "end": v(4.08, -16.37) * mm});
            skLineSegment(sketch, "E385", {"start": v(4.08, -16.37) * mm, "end": v(3.97, -16.24) * mm});
            skLineSegment(sketch, "E386", {"start": v(3.97, -16.24) * mm, "end": v(3.9, -16.18) * mm});
            skLineSegment(sketch, "E387", {"start": v(3.9, -16.18) * mm, "end": v(3.82, -16.12) * mm});
            skLineSegment(sketch, "E388", {"start": v(3.82, -16.12) * mm, "end": v(3.61, -16.1) * mm});
            skLineSegment(sketch, "E389", {"start": v(3.61, -16.1) * mm, "end": v(2.11, -16.36) * mm});
            skLineSegment(sketch, "E390", {"start": v(2.11, -16.36) * mm, "end": v(1.93, -16.46) * mm});
            skLineSegment(sketch, "E391", {"start": v(1.93, -16.46) * mm, "end": v(1.86, -16.54) * mm});
            skLineSegment(sketch, "E392", {"start": v(1.86, -16.54) * mm, "end": v(1.82, -16.62) * mm});
            skLineSegment(sketch, "E393", {"start": v(1.82, -16.62) * mm, "end": v(1.77, -16.78) * mm});
            skLineSegment(sketch, "E394", {"start": v(1.77, -16.78) * mm, "end": v(1.73, -16.93) * mm});
            skLineSegment(sketch, "E395", {"start": v(1.73, -16.93) * mm, "end": v(1.72, -17.08) * mm});
            skLineSegment(sketch, "E396", {"start": v(1.72, -17.08) * mm, "end": v(1.69, -17.4) * mm});
            skLineSegment(sketch, "E397", {"start": v(1.69, -17.4) * mm, "end": v(1.63, -17.7) * mm});
            skLineSegment(sketch, "E398", {"start": v(1.63, -17.7) * mm, "end": v(1.55, -18) * mm});
            skLineSegment(sketch, "E399", {"start": v(1.55, -18) * mm, "end": v(1.45, -18.32) * mm});
            skLineSegment(sketch, "E400", {"start": v(1.45, -18.32) * mm, "end": v(1.34, -18.63) * mm});
            skLineSegment(sketch, "E401", {"start": v(1.34, -18.63) * mm, "end": v(1.21, -18.94) * mm});
            skLineSegment(sketch, "E402", {"start": v(1.21, -18.94) * mm, "end": v(1.07, -19.25) * mm});
            skLineSegment(sketch, "E403", {"start": v(1.07, -19.25) * mm, "end": v(0.96, -19.48) * mm});
            skLineSegment(sketch, "E404", {"start": v(0.96, -19.48) * mm, "end": v(-0.96, -19.48) * mm});
            skLineSegment(sketch, "E405", {"start": v(-0.96, -19.48) * mm, "end": v(-1.07, -19.25) * mm});
            skLineSegment(sketch, "E406", {"start": v(-1.07, -19.25) * mm, "end": v(-1.21, -18.94) * mm});
            skLineSegment(sketch, "E407", {"start": v(-1.21, -18.94) * mm, "end": v(-1.34, -18.63) * mm});
            skLineSegment(sketch, "E408", {"start": v(-1.34, -18.63) * mm, "end": v(-1.45, -18.32) * mm});
            skLineSegment(sketch, "E409", {"start": v(-1.45, -18.32) * mm, "end": v(-1.55, -18) * mm});
            skLineSegment(sketch, "E410", {"start": v(-1.55, -18) * mm, "end": v(-1.63, -17.7) * mm});
            skLineSegment(sketch, "E411", {"start": v(-1.63, -17.7) * mm, "end": v(-1.69, -17.4) * mm});
            skLineSegment(sketch, "E412", {"start": v(-1.69, -17.4) * mm, "end": v(-1.72, -17.08) * mm});
            skLineSegment(sketch, "E413", {"start": v(-1.72, -17.08) * mm, "end": v(-1.73, -16.93) * mm});
            skLineSegment(sketch, "E414", {"start": v(-1.73, -16.93) * mm, "end": v(-1.77, -16.78) * mm});
            skLineSegment(sketch, "E415", {"start": v(-1.77, -16.78) * mm, "end": v(-1.82, -16.62) * mm});
            skLineSegment(sketch, "E416", {"start": v(-1.82, -16.62) * mm, "end": v(-1.86, -16.54) * mm});
            skLineSegment(sketch, "E417", {"start": v(-1.86, -16.54) * mm, "end": v(-1.93, -16.46) * mm});
            skLineSegment(sketch, "E418", {"start": v(-1.93, -16.46) * mm, "end": v(-2.11, -16.36) * mm});
            skLineSegment(sketch, "E419", {"start": v(-2.11, -16.36) * mm, "end": v(-3.61, -16.1) * mm});
            skLineSegment(sketch, "E420", {"start": v(-3.61, -16.1) * mm, "end": v(-3.82, -16.12) * mm});
            skLineSegment(sketch, "E421", {"start": v(-3.82, -16.12) * mm, "end": v(-3.9, -16.18) * mm});
            skLineSegment(sketch, "E422", {"start": v(-3.9, -16.18) * mm, "end": v(-3.97, -16.24) * mm});
            skLineSegment(sketch, "E423", {"start": v(-3.97, -16.24) * mm, "end": v(-4.08, -16.37) * mm});
            skLineSegment(sketch, "E424", {"start": v(-4.08, -16.37) * mm, "end": v(-4.17, -16.5) * mm});
            skLineSegment(sketch, "E425", {"start": v(-4.17, -16.5) * mm, "end": v(-4.23, -16.64) * mm});
            skLineSegment(sketch, "E426", {"start": v(-4.23, -16.64) * mm, "end": v(-4.36, -16.92) * mm});
            skLineSegment(sketch, "E427", {"start": v(-4.36, -16.92) * mm, "end": v(-4.53, -17.19) * mm});
            skLineSegment(sketch, "E428", {"start": v(-4.53, -17.19) * mm, "end": v(-4.7, -17.45) * mm});
            skLineSegment(sketch, "E429", {"start": v(-4.7, -17.45) * mm, "end": v(-4.9, -17.71) * mm});
            skLineSegment(sketch, "E430", {"start": v(-4.9, -17.71) * mm, "end": v(-5.11, -17.96) * mm});
            skLineSegment(sketch, "E431", {"start": v(-5.11, -17.96) * mm, "end": v(-5.34, -18.21) * mm});
            skLineSegment(sketch, "E432", {"start": v(-5.34, -18.21) * mm, "end": v(-5.58, -18.46) * mm});
            skLineSegment(sketch, "E433", {"start": v(-5.58, -18.46) * mm, "end": v(-5.76, -18.64) * mm});
            skLineSegment(sketch, "E434", {"start": v(-5.76, -18.64) * mm, "end": v(-7.56, -17.98) * mm});
            skLineSegment(sketch, "E435", {"start": v(-7.56, -17.98) * mm, "end": v(-7.6, -17.72) * mm});
            skLineSegment(sketch, "E436", {"start": v(-7.6, -17.72) * mm, "end": v(-7.62, -17.38) * mm});
            skLineSegment(sketch, "E437", {"start": v(-7.62, -17.38) * mm, "end": v(-7.63, -17.05) * mm});
            skLineSegment(sketch, "E438", {"start": v(-7.63, -17.05) * mm, "end": v(-7.63, -16.72) * mm});
            skLineSegment(sketch, "E439", {"start": v(-7.63, -16.72) * mm, "end": v(-7.61, -16.4) * mm});
            skLineSegment(sketch, "E440", {"start": v(-7.61, -16.4) * mm, "end": v(-7.58, -16.08) * mm});
            skLineSegment(sketch, "E441", {"start": v(-7.58, -16.08) * mm, "end": v(-7.53, -15.77) * mm});
            skLineSegment(sketch, "E442", {"start": v(-7.53, -15.77) * mm, "end": v(-7.46, -15.47) * mm});
            skLineSegment(sketch, "E443", {"start": v(-7.46, -15.47) * mm, "end": v(-7.42, -15.32) * mm});
            skLineSegment(sketch, "E444", {"start": v(-7.42, -15.32) * mm, "end": v(-7.4, -15.16) * mm});
            skLineSegment(sketch, "E445", {"start": v(-7.4, -15.16) * mm, "end": v(-7.4, -15) * mm});
            skLineSegment(sketch, "E446", {"start": v(-7.4, -15) * mm, "end": v(-7.4, -14.9) * mm});
            skLineSegment(sketch, "E447", {"start": v(-7.4, -14.9) * mm, "end": v(-7.44, -14.8) * mm});
            skLineSegment(sketch, "E448", {"start": v(-7.44, -14.8) * mm, "end": v(-7.58, -14.65) * mm});
            skLineSegment(sketch, "E449", {"start": v(-7.58, -14.65) * mm, "end": v(-8.9, -13.89) * mm});
            skLineSegment(sketch, "E450", {"start": v(-8.9, -13.89) * mm, "end": v(-9.1, -13.85) * mm});
            skLineSegment(sketch, "E451", {"start": v(-9.1, -13.85) * mm, "end": v(-9.2, -13.87) * mm});
            skLineSegment(sketch, "E452", {"start": v(-9.2, -13.87) * mm, "end": v(-9.29, -13.9) * mm});
            skLineSegment(sketch, "E453", {"start": v(-9.29, -13.9) * mm, "end": v(-9.43, -13.99) * mm});
            skLineSegment(sketch, "E454", {"start": v(-9.43, -13.99) * mm, "end": v(-9.56, -14.08) * mm});
            skLineSegment(sketch, "E455", {"start": v(-9.56, -14.08) * mm, "end": v(-9.66, -14.2) * mm});
            skLineSegment(sketch, "E456", {"start": v(-9.66, -14.2) * mm, "end": v(-9.89, -14.4) * mm});
            skLineSegment(sketch, "E457", {"start": v(-9.89, -14.4) * mm, "end": v(-10.13, -14.6) * mm});
            skLineSegment(sketch, "E458", {"start": v(-10.13, -14.6) * mm, "end": v(-10.4, -14.8) * mm});
            skLineSegment(sketch, "E459", {"start": v(-10.4, -14.8) * mm, "end": v(-10.66, -14.97) * mm});
            skLineSegment(sketch, "E460", {"start": v(-10.66, -14.97) * mm, "end": v(-10.95, -15.13) * mm});
            skLineSegment(sketch, "E461", {"start": v(-10.95, -15.13) * mm, "end": v(-11.25, -15.29) * mm});
            skLineSegment(sketch, "E462", {"start": v(-11.25, -15.29) * mm, "end": v(-11.55, -15.44) * mm});
            skLineSegment(sketch, "E463", {"start": v(-11.55, -15.44) * mm, "end": v(-11.8, -15.54) * mm});
            skLineSegment(sketch, "E464", {"start": v(-11.8, -15.54) * mm, "end": v(-13.26, -14.3) * mm});
            skLineSegment(sketch, "E465", {"start": v(-13.26, -14.3) * mm, "end": v(-13.2, -14.06) * mm});
            skLineSegment(sketch, "E466", {"start": v(-13.2, -14.06) * mm, "end": v(-13.1, -13.73) * mm});
            skLineSegment(sketch, "E467", {"start": v(-13.1, -13.73) * mm, "end": v(-13, -13.4) * mm});
            skLineSegment(sketch, "E468", {"start": v(-13, -13.4) * mm, "end": v(-12.89, -13.1) * mm});
            skLineSegment(sketch, "E469", {"start": v(-12.89, -13.1) * mm, "end": v(-12.76, -12.8) * mm});
            skLineSegment(sketch, "E470", {"start": v(-12.76, -12.8) * mm, "end": v(-12.62, -12.51) * mm});
            skLineSegment(sketch, "E471", {"start": v(-12.62, -12.51) * mm, "end": v(-12.47, -12.24) * mm});
            skLineSegment(sketch, "E472", {"start": v(-12.47, -12.24) * mm, "end": v(-12.3, -11.98) * mm});
            skLineSegment(sketch, "E473", {"start": v(-12.3, -11.98) * mm, "end": v(-12.2, -11.86) * mm});
            skLineSegment(sketch, "E474", {"start": v(-12.2, -11.86) * mm, "end": v(-12.14, -11.72) * mm});
            skLineSegment(sketch, "E475", {"start": v(-12.14, -11.72) * mm, "end": v(-12.08, -11.56) * mm});
            skLineSegment(sketch, "E476", {"start": v(-12.08, -11.56) * mm, "end": v(-12.06, -11.47) * mm});
            skLineSegment(sketch, "E477", {"start": v(-12.06, -11.47) * mm, "end": v(-12.05, -11.37) * mm});
            skLineSegment(sketch, "E478", {"start": v(-12.05, -11.37) * mm, "end": v(-12.13, -11.17) * mm});
            skLineSegment(sketch, "E479", {"start": v(-12.13, -11.17) * mm, "end": v(-13.11, -10) * mm});
            skLineSegment(sketch, "E480", {"start": v(-13.11, -10) * mm, "end": v(-13.29, -9.9) * mm});
            skLineSegment(sketch, "E481", {"start": v(-13.29, -9.9) * mm, "end": v(-13.4, -9.88) * mm});
            skLineSegment(sketch, "E482", {"start": v(-13.4, -9.88) * mm, "end": v(-13.48, -9.89) * mm});
            skLineSegment(sketch, "E483", {"start": v(-13.48, -9.89) * mm, "end": v(-13.65, -9.92) * mm});
            skLineSegment(sketch, "E484", {"start": v(-13.65, -9.92) * mm, "end": v(-13.8, -9.96) * mm});
            skLineSegment(sketch, "E485", {"start": v(-13.8, -9.96) * mm, "end": v(-13.93, -10.03) * mm});
            skLineSegment(sketch, "E486", {"start": v(-13.93, -10.03) * mm, "end": v(-14.22, -10.15) * mm});
            skLineSegment(sketch, "E487", {"start": v(-14.22, -10.15) * mm, "end": v(-14.52, -10.26) * mm});
            skLineSegment(sketch, "E488", {"start": v(-14.52, -10.26) * mm, "end": v(-14.82, -10.34) * mm});
            skLineSegment(sketch, "E489", {"start": v(-14.82, -10.34) * mm, "end": v(-15.14, -10.42) * mm});
            skLineSegment(sketch, "E490", {"start": v(-15.14, -10.42) * mm, "end": v(-15.46, -10.48) * mm});
            skLineSegment(sketch, "E491", {"start": v(-15.46, -10.48) * mm, "end": v(-15.8, -10.52) * mm});
            skLineSegment(sketch, "E492", {"start": v(-15.8, -10.52) * mm, "end": v(-16.14, -10.55) * mm});
            skLineSegment(sketch, "E493", {"start": v(-16.14, -10.55) * mm, "end": v(-16.4, -10.57) * mm});
            skLineSegment(sketch, "E494", {"start": v(-16.4, -10.57) * mm, "end": v(-17.35, -8.91) * mm});
            skLineSegment(sketch, "E495", {"start": v(-17.35, -8.91) * mm, "end": v(-17.2, -8.7) * mm});
            skLineSegment(sketch, "E496", {"start": v(-17.2, -8.7) * mm, "end": v(-17.01, -8.42) * mm});
            skLineSegment(sketch, "E497", {"start": v(-17.01, -8.42) * mm, "end": v(-16.8, -8.15) * mm});
            skLineSegment(sketch, "E498", {"start": v(-16.8, -8.15) * mm, "end": v(-16.6, -7.9) * mm});
            skLineSegment(sketch, "E499", {"start": v(-16.6, -7.9) * mm, "end": v(-16.37, -7.66) * mm});
            skLineSegment(sketch, "E500", {"start": v(-16.37, -7.66) * mm, "end": v(-16.14, -7.44) * mm});
            skLineSegment(sketch, "E501", {"start": v(-16.14, -7.44) * mm, "end": v(-15.9, -7.24) * mm});
            skLineSegment(sketch, "E502", {"start": v(-15.9, -7.24) * mm, "end": v(-15.66, -7.05) * mm});
            skLineSegment(sketch, "E503", {"start": v(-15.66, -7.05) * mm, "end": v(-15.53, -6.97) * mm});
            skLineSegment(sketch, "E504", {"start": v(-15.53, -6.97) * mm, "end": v(-15.41, -6.86) * mm});
            skLineSegment(sketch, "E505", {"start": v(-15.41, -6.86) * mm, "end": v(-15.3, -6.73) * mm});
            skLineSegment(sketch, "E506", {"start": v(-15.3, -6.73) * mm, "end": v(-15.26, -6.65) * mm});
            skLineSegment(sketch, "E507", {"start": v(-15.26, -6.65) * mm, "end": v(-15.22, -6.56) * mm});
            skLineSegment(sketch, "E508", {"start": v(-15.22, -6.56) * mm, "end": v(-15.22, -6.35) * mm});
            skLineSegment(sketch, "E509", {"start": v(-15.22, -6.35) * mm, "end": v(-15.74, -4.92) * mm});
            skLineSegment(sketch, "E510", {"start": v(-15.74, -4.92) * mm, "end": v(-15.87, -4.76) * mm});
            skLineSegment(sketch, "E511", {"start": v(-15.87, -4.76) * mm, "end": v(-15.96, -4.7) * mm});
            skLineSegment(sketch, "E512", {"start": v(-15.96, -4.7) * mm, "end": v(-16.05, -4.68) * mm});
            skLineSegment(sketch, "E513", {"start": v(-16.05, -4.68) * mm, "end": v(-16.22, -4.65) * mm});
            skLineSegment(sketch, "E514", {"start": v(-16.22, -4.65) * mm, "end": v(-16.37, -4.64) * mm});
            skLineSegment(sketch, "E515", {"start": v(-16.37, -4.64) * mm, "end": v(-16.53, -4.66) * mm});
            skLineSegment(sketch, "E516", {"start": v(-16.53, -4.66) * mm, "end": v(-16.83, -4.68) * mm});
            skLineSegment(sketch, "E517", {"start": v(-16.83, -4.68) * mm, "end": v(-17.15, -4.67) * mm});
            skLineSegment(sketch, "E518", {"start": v(-17.15, -4.67) * mm, "end": v(-17.47, -4.65) * mm});
            skLineSegment(sketch, "E519", {"start": v(-17.47, -4.65) * mm, "end": v(-17.79, -4.61) * mm});
            skLineSegment(sketch, "E520", {"start": v(-17.79, -4.61) * mm, "end": v(-18.11, -4.55) * mm});
            skLineSegment(sketch, "E521", {"start": v(-18.11, -4.55) * mm, "end": v(-18.44, -4.48) * mm});
            skLineSegment(sketch, "E522", {"start": v(-18.44, -4.48) * mm, "end": v(-18.77, -4.4) * mm});
            skLineSegment(sketch, "E523", {"start": v(-18.77, -4.4) * mm, "end": v(-19.02, -4.33) * mm});
            skLineSegment(sketch, "E524", {"start": v(-19.02, -4.33) * mm, "end": v(-19.35, -2.44) * mm});
            skLineSegment(sketch, "E525", {"start": v(-19.35, -2.44) * mm, "end": v(-19.15, -2.29) * mm});
            skLineSegment(sketch, "E526", {"start": v(-19.15, -2.29) * mm, "end": v(-18.86, -2.1) * mm});
            skLineSegment(sketch, "E527", {"start": v(-18.86, -2.1) * mm, "end": v(-18.58, -1.92) * mm});
            skLineSegment(sketch, "E528", {"start": v(-18.58, -1.92) * mm, "end": v(-18.3, -1.75) * mm});
            skLineSegment(sketch, "E529", {"start": v(-18.3, -1.75) * mm, "end": v(-18, -1.6) * mm});
            skLineSegment(sketch, "E530", {"start": v(-18, -1.6) * mm, "end": v(-17.71, -1.47) * mm});
            skLineSegment(sketch, "E531", {"start": v(-17.71, -1.47) * mm, "end": v(-17.42, -1.36) * mm});
            skLineSegment(sketch, "E532", {"start": v(-17.42, -1.36) * mm, "end": v(-17.12, -1.27) * mm});
            skLineSegment(sketch, "E533", {"start": v(-17.12, -1.27) * mm, "end": v(-16.98, -1.24) * mm});
            skLineSegment(sketch, "E534", {"start": v(-16.98, -1.24) * mm, "end": v(-16.83, -1.17) * mm});
            skLineSegment(sketch, "E535", {"start": v(-16.83, -1.17) * mm, "end": v(-16.68, -1.1) * mm});
            skLineSegment(sketch, "E536", {"start": v(-16.68, -1.1) * mm, "end": v(-16.61, -1.04) * mm});
            skLineSegment(sketch, "E537", {"start": v(-16.61, -1.04) * mm, "end": v(-16.54, -0.96) * mm});
            skLineSegment(sketch, "E538", {"start": v(-16.54, -0.96) * mm, "end": v(-16.48, -0.76) * mm});
            skLineSegment(sketch, "E539", {"start": v(-16.48, -0.76) * mm, "end": v(-16.48, 0.76) * mm});
            skPoint(sketch, "E540", {"position": v(0, 0) * mm});
            skLineSegment(sketch, "E541", {"start": v(-16.48, 0.76) * mm, "end": v(16.48, -0.76) * mm, "construction": true});
            skLineSegment(sketch, "E542", {"start": v(19.35, 2.44) * mm, "end": v(-19.35, -2.44) * mm, "construction": true});
            skLineSegment(sketch, "E543", {"start": v(-16.48, -0.76) * mm, "end": v(-19.02, -4.33) * mm, "construction": true});
            skSolve(sketch);
        }
        {
            var Q0;
            Q0=makeQuery(id+"F0.imprint","IMPRINT",FACE,{"disambiguationData":[TD([[makeQuery(id+"F0.imprint","IMPRINT",EDGE,{"derivedFrom":sQuery(id+"F0.wireOp",EDGE,"E0")}),-1.0]])]});
            extrude(context, id + "F1", {"entities" : qUnion([Q0]), "depth" : 2.9 * mm, "offsetDistance" : 25 * mm});
        }
        {
            var Q0;
            Q0=makeQuery(id+"F1.opExtrude","CAP_FACE",FACE,{"disambiguationData":[OSD([sQuery(id+"F0.wireOp",EDGE,"E0"),sQuery(id+"F0.wireOp",EDGE,"E1"),sQuery(id+"F0.wireOp",EDGE,"E2"),sQuery(id+"F0.wireOp",EDGE,"E3"),sQuery(id+"F0.wireOp",EDGE,"E4"),sQuery(id+"F0.wireOp",EDGE,"E5"),sQuery(id+"F0.wireOp",EDGE,"E6"),sQuery(id+"F0.wireOp",EDGE,"E7"),sQuery(id+"F0.wireOp",EDGE,"E8"),sQuery(id+"F0.wireOp",EDGE,"E9"),sQuery(id+"F0.wireOp",EDGE,"E10"),sQuery(id+"F0.wireOp",EDGE,"E11"),sQuery(id+"F0.wireOp",EDGE,"E12"),sQuery(id+"F0.wireOp",EDGE,"E13"),sQuery(id+"F0.wireOp",EDGE,"E14"),sQuery(id+"F0.wireOp",EDGE,"E15"),sQuery(id+"F0.wireOp",EDGE,"E16"),sQuery(id+"F0.wireOp",EDGE,"E17"),sQuery(id+"F0.wireOp",EDGE,"E18"),sQuery(id+"F0.wireOp",EDGE,"E19"),sQuery(id+"F0.wireOp",EDGE,"E20"),sQuery(id+"F0.wireOp",EDGE,"E21"),sQuery(id+"F0.wireOp",EDGE,"E22"),sQuery(id+"F0.wireOp",EDGE,"E23"),sQuery(id+"F0.wireOp",EDGE,"E24"),sQuery(id+"F0.wireOp",EDGE,"E25"),sQuery(id+"F0.wireOp",EDGE,"E26"),sQuery(id+"F0.wireOp",EDGE,"E27"),sQuery(id+"F0.wireOp",EDGE,"E28"),sQuery(id+"F0.wireOp",EDGE,"E29"),sQuery(id+"F0.wireOp",EDGE,"E30"),sQuery(id+"F0.wireOp",EDGE,"E31"),sQuery(id+"F0.wireOp",EDGE,"E32"),sQuery(id+"F0.wireOp",EDGE,"E33"),sQuery(id+"F0.wireOp",EDGE,"E34"),sQuery(id+"F0.wireOp",EDGE,"E35"),sQuery(id+"F0.wireOp",EDGE,"E36"),sQuery(id+"F0.wireOp",EDGE,"E37"),sQuery(id+"F0.wireOp",EDGE,"E38"),sQuery(id+"F0.wireOp",EDGE,"E39"),sQuery(id+"F0.wireOp",EDGE,"E40"),sQuery(id+"F0.wireOp",EDGE,"E41"),sQuery(id+"F0.wireOp",EDGE,"E42"),sQuery(id+"F0.wireOp",EDGE,"E43"),sQuery(id+"F0.wireOp",EDGE,"E44"),sQuery(id+"F0.wireOp",EDGE,"E45"),sQuery(id+"F0.wireOp",EDGE,"E46"),sQuery(id+"F0.wireOp",EDGE,"E47"),sQuery(id+"F0.wireOp",EDGE,"E48"),sQuery(id+"F0.wireOp",EDGE,"E49"),sQuery(id+"F0.wireOp",EDGE,"E50"),sQuery(id+"F0.wireOp",EDGE,"E51"),sQuery(id+"F0.wireOp",EDGE,"E52"),sQuery(id+"F0.wireOp",EDGE,"E53"),sQuery(id+"F0.wireOp",EDGE,"E54"),sQuery(id+"F0.wireOp",EDGE,"E55"),sQuery(id+"F0.wireOp",EDGE,"E56"),sQuery(id+"F0.wireOp",EDGE,"E57"),sQuery(id+"F0.wireOp",EDGE,"E58"),sQuery(id+"F0.wireOp",EDGE,"E59"),sQuery(id+"F0.wireOp",EDGE,"E60"),sQuery(id+"F0.wireOp",EDGE,"E61"),sQuery(id+"F0.wireOp",EDGE,"E62"),sQuery(id+"F0.wireOp",EDGE,"E63"),sQuery(id+"F0.wireOp",EDGE,"E64"),sQuery(id+"F0.wireOp",EDGE,"E65"),sQuery(id+"F0.wireOp",EDGE,"E66"),sQuery(id+"F0.wireOp",EDGE,"E67"),sQuery(id+"F0.wireOp",EDGE,"E68"),sQuery(id+"F0.wireOp",EDGE,"E69"),sQuery(id+"F0.wireOp",EDGE,"E70"),sQuery(id+"F0.wireOp",EDGE,"E71"),sQuery(id+"F0.wireOp",EDGE,"E72"),sQuery(id+"F0.wireOp",EDGE,"E73"),sQuery(id+"F0.wireOp",EDGE,"E74"),sQuery(id+"F0.wireOp",EDGE,"E75"),sQuery(id+"F0.wireOp",EDGE,"E76"),sQuery(id+"F0.wireOp",EDGE,"E77"),sQuery(id+"F0.wireOp",EDGE,"E78"),sQuery(id+"F0.wireOp",EDGE,"E79"),sQuery(id+"F0.wireOp",EDGE,"E80"),sQuery(id+"F0.wireOp",EDGE,"E81"),sQuery(id+"F0.wireOp",EDGE,"E82"),sQuery(id+"F0.wireOp",EDGE,"E83"),sQuery(id+"F0.wireOp",EDGE,"E84"),sQuery(id+"F0.wireOp",EDGE,"E85"),sQuery(id+"F0.wireOp",EDGE,"E86"),sQuery(id+"F0.wireOp",EDGE,"E87"),sQuery(id+"F0.wireOp",EDGE,"E88"),sQuery(id+"F0.wireOp",EDGE,"E89"),sQuery(id+"F0.wireOp",EDGE,"E90"),sQuery(id+"F0.wireOp",EDGE,"E91"),sQuery(id+"F0.wireOp",EDGE,"E92"),sQuery(id+"F0.wireOp",EDGE,"E93"),sQuery(id+"F0.wireOp",EDGE,"E94"),sQuery(id+"F0.wireOp",EDGE,"E95"),sQuery(id+"F0.wireOp",EDGE,"E96"),sQuery(id+"F0.wireOp",EDGE,"E97"),sQuery(id+"F0.wireOp",EDGE,"E98"),sQuery(id+"F0.wireOp",EDGE,"E99"),sQuery(id+"F0.wireOp",EDGE,"E100"),sQuery(id+"F0.wireOp",EDGE,"E101"),sQuery(id+"F0.wireOp",EDGE,"E102"),sQuery(id+"F0.wireOp",EDGE,"E103"),sQuery(id+"F0.wireOp",EDGE,"E104"),sQuery(id+"F0.wireOp",EDGE,"E105"),sQuery(id+"F0.wireOp",EDGE,"E106"),sQuery(id+"F0.wireOp",EDGE,"E107"),sQuery(id+"F0.wireOp",EDGE,"E108"),sQuery(id+"F0.wireOp",EDGE,"E109"),sQuery(id+"F0.wireOp",EDGE,"E110"),sQuery(id+"F0.wireOp",EDGE,"E111"),sQuery(id+"F0.wireOp",EDGE,"E112"),sQuery(id+"F0.wireOp",EDGE,"E113"),sQuery(id+"F0.wireOp",EDGE,"E114"),sQuery(id+"F0.wireOp",EDGE,"E115"),sQuery(id+"F0.wireOp",EDGE,"E116"),sQuery(id+"F0.wireOp",EDGE,"E117"),sQuery(id+"F0.wireOp",EDGE,"E118"),sQuery(id+"F0.wireOp",EDGE,"E119"),sQuery(id+"F0.wireOp",EDGE,"E120"),sQuery(id+"F0.wireOp",EDGE,"E121"),sQuery(id+"F0.wireOp",EDGE,"E122"),sQuery(id+"F0.wireOp",EDGE,"E123"),sQuery(id+"F0.wireOp",EDGE,"E124"),sQuery(id+"F0.wireOp",EDGE,"E125"),sQuery(id+"F0.wireOp",EDGE,"E126"),sQuery(id+"F0.wireOp",EDGE,"E127"),sQuery(id+"F0.wireOp",EDGE,"E128"),sQuery(id+"F0.wireOp",EDGE,"E129"),sQuery(id+"F0.wireOp",EDGE,"E130"),sQuery(id+"F0.wireOp",EDGE,"E131"),sQuery(id+"F0.wireOp",EDGE,"E132"),sQuery(id+"F0.wireOp",EDGE,"E133"),sQuery(id+"F0.wireOp",EDGE,"E134"),sQuery(id+"F0.wireOp",EDGE,"E135"),sQuery(id+"F0.wireOp",EDGE,"E136"),sQuery(id+"F0.wireOp",EDGE,"E137"),sQuery(id+"F0.wireOp",EDGE,"E138"),sQuery(id+"F0.wireOp",EDGE,"E139"),sQuery(id+"F0.wireOp",EDGE,"E140"),sQuery(id+"F0.wireOp",EDGE,"E141"),sQuery(id+"F0.wireOp",EDGE,"E142"),sQuery(id+"F0.wireOp",EDGE,"E143"),sQuery(id+"F0.wireOp",EDGE,"E144"),sQuery(id+"F0.wireOp",EDGE,"E145"),sQuery(id+"F0.wireOp",EDGE,"E146"),sQuery(id+"F0.wireOp",EDGE,"E147"),sQuery(id+"F0.wireOp",EDGE,"E148"),sQuery(id+"F0.wireOp",EDGE,"E149"),sQuery(id+"F0.wireOp",EDGE,"E150"),sQuery(id+"F0.wireOp",EDGE,"E151"),sQuery(id+"F0.wireOp",EDGE,"E152"),sQuery(id+"F0.wireOp",EDGE,"E153"),sQuery(id+"F0.wireOp",EDGE,"E154"),sQuery(id+"F0.wireOp",EDGE,"E155"),sQuery(id+"F0.wireOp",EDGE,"E156"),sQuery(id+"F0.wireOp",EDGE,"E157"),sQuery(id+"F0.wireOp",EDGE,"E158"),sQuery(id+"F0.wireOp",EDGE,"E159"),sQuery(id+"F0.wireOp",EDGE,"E160"),sQuery(id+"F0.wireOp",EDGE,"E161"),sQuery(id+"F0.wireOp",EDGE,"E162"),sQuery(id+"F0.wireOp",EDGE,"E163"),sQuery(id+"F0.wireOp",EDGE,"E164"),sQuery(id+"F0.wireOp",EDGE,"E165"),sQuery(id+"F0.wireOp",EDGE,"E166"),sQuery(id+"F0.wireOp",EDGE,"E167"),sQuery(id+"F0.wireOp",EDGE,"E168"),sQuery(id+"F0.wireOp",EDGE,"E169"),sQuery(id+"F0.wireOp",EDGE,"E170"),sQuery(id+"F0.wireOp",EDGE,"E171"),sQuery(id+"F0.wireOp",EDGE,"E172"),sQuery(id+"F0.wireOp",EDGE,"E173"),sQuery(id+"F0.wireOp",EDGE,"E174"),sQuery(id+"F0.wireOp",EDGE,"E175"),sQuery(id+"F0.wireOp",EDGE,"E176"),sQuery(id+"F0.wireOp",EDGE,"E177"),sQuery(id+"F0.wireOp",EDGE,"E178"),sQuery(id+"F0.wireOp",EDGE,"E179"),sQuery(id+"F0.wireOp",EDGE,"E180"),sQuery(id+"F0.wireOp",EDGE,"E181"),sQuery(id+"F0.wireOp",EDGE,"E182"),sQuery(id+"F0.wireOp",EDGE,"E183"),sQuery(id+"F0.wireOp",EDGE,"E184"),sQuery(id+"F0.wireOp",EDGE,"E185"),sQuery(id+"F0.wireOp",EDGE,"E186"),sQuery(id+"F0.wireOp",EDGE,"E187"),sQuery(id+"F0.wireOp",EDGE,"E188"),sQuery(id+"F0.wireOp",EDGE,"E189"),sQuery(id+"F0.wireOp",EDGE,"E190"),sQuery(id+"F0.wireOp",EDGE,"E191"),sQuery(id+"F0.wireOp",EDGE,"E192"),sQuery(id+"F0.wireOp",EDGE,"E193"),sQuery(id+"F0.wireOp",EDGE,"E194"),sQuery(id+"F0.wireOp",EDGE,"E195"),sQuery(id+"F0.wireOp",EDGE,"E196"),sQuery(id+"F0.wireOp",EDGE,"E197"),sQuery(id+"F0.wireOp",EDGE,"E198"),sQuery(id+"F0.wireOp",EDGE,"E199"),sQuery(id+"F0.wireOp",EDGE,"E200"),sQuery(id+"F0.wireOp",EDGE,"E201"),sQuery(id+"F0.wireOp",EDGE,"E202"),sQuery(id+"F0.wireOp",EDGE,"E203"),sQuery(id+"F0.wireOp",EDGE,"E204"),sQuery(id+"F0.wireOp",EDGE,"E205"),sQuery(id+"F0.wireOp",EDGE,"E206"),sQuery(id+"F0.wireOp",EDGE,"E207"),sQuery(id+"F0.wireOp",EDGE,"E208"),sQuery(id+"F0.wireOp",EDGE,"E209"),sQuery(id+"F0.wireOp",EDGE,"E210"),sQuery(id+"F0.wireOp",EDGE,"E211"),sQuery(id+"F0.wireOp",EDGE,"E212"),sQuery(id+"F0.wireOp",EDGE,"E213"),sQuery(id+"F0.wireOp",EDGE,"E214"),sQuery(id+"F0.wireOp",EDGE,"E215"),sQuery(id+"F0.wireOp",EDGE,"E216"),sQuery(id+"F0.wireOp",EDGE,"E217"),sQuery(id+"F0.wireOp",EDGE,"E218"),sQuery(id+"F0.wireOp",EDGE,"E219"),sQuery(id+"F0.wireOp",EDGE,"E220"),sQuery(id+"F0.wireOp",EDGE,"E221"),sQuery(id+"F0.wireOp",EDGE,"E222"),sQuery(id+"F0.wireOp",EDGE,"E223"),sQuery(id+"F0.wireOp",EDGE,"E224"),sQuery(id+"F0.wireOp",EDGE,"E225"),sQuery(id+"F0.wireOp",EDGE,"E226"),sQuery(id+"F0.wireOp",EDGE,"E227"),sQuery(id+"F0.wireOp",EDGE,"E228"),sQuery(id+"F0.wireOp",EDGE,"E229"),sQuery(id+"F0.wireOp",EDGE,"E230"),sQuery(id+"F0.wireOp",EDGE,"E231"),sQuery(id+"F0.wireOp",EDGE,"E232"),sQuery(id+"F0.wireOp",EDGE,"E233"),sQuery(id+"F0.wireOp",EDGE,"E234"),sQuery(id+"F0.wireOp",EDGE,"E235"),sQuery(id+"F0.wireOp",EDGE,"E236"),sQuery(id+"F0.wireOp",EDGE,"E237"),sQuery(id+"F0.wireOp",EDGE,"E238"),sQuery(id+"F0.wireOp",EDGE,"E239"),sQuery(id+"F0.wireOp",EDGE,"E240"),sQuery(id+"F0.wireOp",EDGE,"E241"),sQuery(id+"F0.wireOp",EDGE,"E242"),sQuery(id+"F0.wireOp",EDGE,"E243"),sQuery(id+"F0.wireOp",EDGE,"E244"),sQuery(id+"F0.wireOp",EDGE,"E245"),sQuery(id+"F0.wireOp",EDGE,"E246"),sQuery(id+"F0.wireOp",EDGE,"E247"),sQuery(id+"F0.wireOp",EDGE,"E248"),sQuery(id+"F0.wireOp",EDGE,"E249"),sQuery(id+"F0.wireOp",EDGE,"E250"),sQuery(id+"F0.wireOp",EDGE,"E251"),sQuery(id+"F0.wireOp",EDGE,"E252"),sQuery(id+"F0.wireOp",EDGE,"E253"),sQuery(id+"F0.wireOp",EDGE,"E254"),sQuery(id+"F0.wireOp",EDGE,"E255"),sQuery(id+"F0.wireOp",EDGE,"E256"),sQuery(id+"F0.wireOp",EDGE,"E257"),sQuery(id+"F0.wireOp",EDGE,"E258"),sQuery(id+"F0.wireOp",EDGE,"E259"),sQuery(id+"F0.wireOp",EDGE,"E260"),sQuery(id+"F0.wireOp",EDGE,"E261"),sQuery(id+"F0.wireOp",EDGE,"E262"),sQuery(id+"F0.wireOp",EDGE,"E263"),sQuery(id+"F0.wireOp",EDGE,"E264"),sQuery(id+"F0.wireOp",EDGE,"E265"),sQuery(id+"F0.wireOp",EDGE,"E266"),sQuery(id+"F0.wireOp",EDGE,"E267"),sQuery(id+"F0.wireOp",EDGE,"E268"),sQuery(id+"F0.wireOp",EDGE,"E269"),sQuery(id+"F0.wireOp",EDGE,"E270"),sQuery(id+"F0.wireOp",EDGE,"E271"),sQuery(id+"F0.wireOp",EDGE,"E272"),sQuery(id+"F0.wireOp",EDGE,"E273"),sQuery(id+"F0.wireOp",EDGE,"E274"),sQuery(id+"F0.wireOp",EDGE,"E275"),sQuery(id+"F0.wireOp",EDGE,"E276"),sQuery(id+"F0.wireOp",EDGE,"E277"),sQuery(id+"F0.wireOp",EDGE,"E278"),sQuery(id+"F0.wireOp",EDGE,"E279"),sQuery(id+"F0.wireOp",EDGE,"E280"),sQuery(id+"F0.wireOp",EDGE,"E281"),sQuery(id+"F0.wireOp",EDGE,"E282"),sQuery(id+"F0.wireOp",EDGE,"E283"),sQuery(id+"F0.wireOp",EDGE,"E284"),sQuery(id+"F0.wireOp",EDGE,"E285"),sQuery(id+"F0.wireOp",EDGE,"E286"),sQuery(id+"F0.wireOp",EDGE,"E287"),sQuery(id+"F0.wireOp",EDGE,"E288"),sQuery(id+"F0.wireOp",EDGE,"E289"),sQuery(id+"F0.wireOp",EDGE,"E290"),sQuery(id+"F0.wireOp",EDGE,"E291"),sQuery(id+"F0.wireOp",EDGE,"E292"),sQuery(id+"F0.wireOp",EDGE,"E293"),sQuery(id+"F0.wireOp",EDGE,"E294"),sQuery(id+"F0.wireOp",EDGE,"E295"),sQuery(id+"F0.wireOp",EDGE,"E296"),sQuery(id+"F0.wireOp",EDGE,"E297"),sQuery(id+"F0.wireOp",EDGE,"E298"),sQuery(id+"F0.wireOp",EDGE,"E299"),sQuery(id+"F0.wireOp",EDGE,"E300"),sQuery(id+"F0.wireOp",EDGE,"E301"),sQuery(id+"F0.wireOp",EDGE,"E302"),sQuery(id+"F0.wireOp",EDGE,"E303"),sQuery(id+"F0.wireOp",EDGE,"E304"),sQuery(id+"F0.wireOp",EDGE,"E305"),sQuery(id+"F0.wireOp",EDGE,"E306"),sQuery(id+"F0.wireOp",EDGE,"E307"),sQuery(id+"F0.wireOp",EDGE,"E308"),sQuery(id+"F0.wireOp",EDGE,"E309"),sQuery(id+"F0.wireOp",EDGE,"E310"),sQuery(id+"F0.wireOp",EDGE,"E311"),sQuery(id+"F0.wireOp",EDGE,"E312"),sQuery(id+"F0.wireOp",EDGE,"E313"),sQuery(id+"F0.wireOp",EDGE,"E314"),sQuery(id+"F0.wireOp",EDGE,"E315"),sQuery(id+"F0.wireOp",EDGE,"E316"),sQuery(id+"F0.wireOp",EDGE,"E317"),sQuery(id+"F0.wireOp",EDGE,"E318"),sQuery(id+"F0.wireOp",EDGE,"E319"),sQuery(id+"F0.wireOp",EDGE,"E320"),sQuery(id+"F0.wireOp",EDGE,"E321"),sQuery(id+"F0.wireOp",EDGE,"E322"),sQuery(id+"F0.wireOp",EDGE,"E323"),sQuery(id+"F0.wireOp",EDGE,"E324"),sQuery(id+"F0.wireOp",EDGE,"E325"),sQuery(id+"F0.wireOp",EDGE,"E326"),sQuery(id+"F0.wireOp",EDGE,"E327"),sQuery(id+"F0.wireOp",EDGE,"E328"),sQuery(id+"F0.wireOp",EDGE,"E329"),sQuery(id+"F0.wireOp",EDGE,"E330"),sQuery(id+"F0.wireOp",EDGE,"E331"),sQuery(id+"F0.wireOp",EDGE,"E332"),sQuery(id+"F0.wireOp",EDGE,"E333"),sQuery(id+"F0.wireOp",EDGE,"E334"),sQuery(id+"F0.wireOp",EDGE,"E335"),sQuery(id+"F0.wireOp",EDGE,"E336"),sQuery(id+"F0.wireOp",EDGE,"E337"),sQuery(id+"F0.wireOp",EDGE,"E338"),sQuery(id+"F0.wireOp",EDGE,"E339"),sQuery(id+"F0.wireOp",EDGE,"E340"),sQuery(id+"F0.wireOp",EDGE,"E341"),sQuery(id+"F0.wireOp",EDGE,"E342"),sQuery(id+"F0.wireOp",EDGE,"E343"),sQuery(id+"F0.wireOp",EDGE,"E344"),sQuery(id+"F0.wireOp",EDGE,"E345"),sQuery(id+"F0.wireOp",EDGE,"E346"),sQuery(id+"F0.wireOp",EDGE,"E347"),sQuery(id+"F0.wireOp",EDGE,"E348"),sQuery(id+"F0.wireOp",EDGE,"E349"),sQuery(id+"F0.wireOp",EDGE,"E350"),sQuery(id+"F0.wireOp",EDGE,"E351"),sQuery(id+"F0.wireOp",EDGE,"E352"),sQuery(id+"F0.wireOp",EDGE,"E353"),sQuery(id+"F0.wireOp",EDGE,"E354"),sQuery(id+"F0.wireOp",EDGE,"E355"),sQuery(id+"F0.wireOp",EDGE,"E356"),sQuery(id+"F0.wireOp",EDGE,"E357"),sQuery(id+"F0.wireOp",EDGE,"E358"),sQuery(id+"F0.wireOp",EDGE,"E359"),sQuery(id+"F0.wireOp",EDGE,"E360"),sQuery(id+"F0.wireOp",EDGE,"E361"),sQuery(id+"F0.wireOp",EDGE,"E362"),sQuery(id+"F0.wireOp",EDGE,"E363"),sQuery(id+"F0.wireOp",EDGE,"E364"),sQuery(id+"F0.wireOp",EDGE,"E365"),sQuery(id+"F0.wireOp",EDGE,"E366"),sQuery(id+"F0.wireOp",EDGE,"E367"),sQuery(id+"F0.wireOp",EDGE,"E368"),sQuery(id+"F0.wireOp",EDGE,"E369"),sQuery(id+"F0.wireOp",EDGE,"E370"),sQuery(id+"F0.wireOp",EDGE,"E371"),sQuery(id+"F0.wireOp",EDGE,"E372"),sQuery(id+"F0.wireOp",EDGE,"E373"),sQuery(id+"F0.wireOp",EDGE,"E374"),sQuery(id+"F0.wireOp",EDGE,"E375"),sQuery(id+"F0.wireOp",EDGE,"E376"),sQuery(id+"F0.wireOp",EDGE,"E377"),sQuery(id+"F0.wireOp",EDGE,"E378"),sQuery(id+"F0.wireOp",EDGE,"E379"),sQuery(id+"F0.wireOp",EDGE,"E380"),sQuery(id+"F0.wireOp",EDGE,"E381"),sQuery(id+"F0.wireOp",EDGE,"E382"),sQuery(id+"F0.wireOp",EDGE,"E383"),sQuery(id+"F0.wireOp",EDGE,"E384"),sQuery(id+"F0.wireOp",EDGE,"E385"),sQuery(id+"F0.wireOp",EDGE,"E386"),sQuery(id+"F0.wireOp",EDGE,"E387"),sQuery(id+"F0.wireOp",EDGE,"E388"),sQuery(id+"F0.wireOp",EDGE,"E389"),sQuery(id+"F0.wireOp",EDGE,"E390"),sQuery(id+"F0.wireOp",EDGE,"E391"),sQuery(id+"F0.wireOp",EDGE,"E392"),sQuery(id+"F0.wireOp",EDGE,"E393"),sQuery(id+"F0.wireOp",EDGE,"E394"),sQuery(id+"F0.wireOp",EDGE,"E395"),sQuery(id+"F0.wireOp",EDGE,"E396"),sQuery(id+"F0.wireOp",EDGE,"E397"),sQuery(id+"F0.wireOp",EDGE,"E398"),sQuery(id+"F0.wireOp",EDGE,"E399"),sQuery(id+"F0.wireOp",EDGE,"E400"),sQuery(id+"F0.wireOp",EDGE,"E401"),sQuery(id+"F0.wireOp",EDGE,"E402"),sQuery(id+"F0.wireOp",EDGE,"E403"),sQuery(id+"F0.wireOp",EDGE,"E404"),sQuery(id+"F0.wireOp",EDGE,"E405"),sQuery(id+"F0.wireOp",EDGE,"E406"),sQuery(id+"F0.wireOp",EDGE,"E407"),sQuery(id+"F0.wireOp",EDGE,"E408"),sQuery(id+"F0.wireOp",EDGE,"E409"),sQuery(id+"F0.wireOp",EDGE,"E410"),sQuery(id+"F0.wireOp",EDGE,"E411"),sQuery(id+"F0.wireOp",EDGE,"E412"),sQuery(id+"F0.wireOp",EDGE,"E413"),sQuery(id+"F0.wireOp",EDGE,"E414"),sQuery(id+"F0.wireOp",EDGE,"E415"),sQuery(id+"F0.wireOp",EDGE,"E416"),sQuery(id+"F0.wireOp",EDGE,"E417"),sQuery(id+"F0.wireOp",EDGE,"E418"),sQuery(id+"F0.wireOp",EDGE,"E419"),sQuery(id+"F0.wireOp",EDGE,"E420"),sQuery(id+"F0.wireOp",EDGE,"E421"),sQuery(id+"F0.wireOp",EDGE,"E422"),sQuery(id+"F0.wireOp",EDGE,"E423"),sQuery(id+"F0.wireOp",EDGE,"E424"),sQuery(id+"F0.wireOp",EDGE,"E425"),sQuery(id+"F0.wireOp",EDGE,"E426"),sQuery(id+"F0.wireOp",EDGE,"E427"),sQuery(id+"F0.wireOp",EDGE,"E428"),sQuery(id+"F0.wireOp",EDGE,"E429"),sQuery(id+"F0.wireOp",EDGE,"E430"),sQuery(id+"F0.wireOp",EDGE,"E431"),sQuery(id+"F0.wireOp",EDGE,"E432"),sQuery(id+"F0.wireOp",EDGE,"E433"),sQuery(id+"F0.wireOp",EDGE,"E434"),sQuery(id+"F0.wireOp",EDGE,"E435"),sQuery(id+"F0.wireOp",EDGE,"E436"),sQuery(id+"F0.wireOp",EDGE,"E437"),sQuery(id+"F0.wireOp",EDGE,"E438"),sQuery(id+"F0.wireOp",EDGE,"E439"),sQuery(id+"F0.wireOp",EDGE,"E440"),sQuery(id+"F0.wireOp",EDGE,"E441"),sQuery(id+"F0.wireOp",EDGE,"E442"),sQuery(id+"F0.wireOp",EDGE,"E443"),sQuery(id+"F0.wireOp",EDGE,"E444"),sQuery(id+"F0.wireOp",EDGE,"E445"),sQuery(id+"F0.wireOp",EDGE,"E446"),sQuery(id+"F0.wireOp",EDGE,"E447"),sQuery(id+"F0.wireOp",EDGE,"E448"),sQuery(id+"F0.wireOp",EDGE,"E449"),sQuery(id+"F0.wireOp",EDGE,"E450"),sQuery(id+"F0.wireOp",EDGE,"E451"),sQuery(id+"F0.wireOp",EDGE,"E452"),sQuery(id+"F0.wireOp",EDGE,"E453"),sQuery(id+"F0.wireOp",EDGE,"E454"),sQuery(id+"F0.wireOp",EDGE,"E455"),sQuery(id+"F0.wireOp",EDGE,"E456"),sQuery(id+"F0.wireOp",EDGE,"E457"),sQuery(id+"F0.wireOp",EDGE,"E458"),sQuery(id+"F0.wireOp",EDGE,"E459"),sQuery(id+"F0.wireOp",EDGE,"E460"),sQuery(id+"F0.wireOp",EDGE,"E461"),sQuery(id+"F0.wireOp",EDGE,"E462"),sQuery(id+"F0.wireOp",EDGE,"E463"),sQuery(id+"F0.wireOp",EDGE,"E464"),sQuery(id+"F0.wireOp",EDGE,"E465"),sQuery(id+"F0.wireOp",EDGE,"E466"),sQuery(id+"F0.wireOp",EDGE,"E467"),sQuery(id+"F0.wireOp",EDGE,"E468"),sQuery(id+"F0.wireOp",EDGE,"E469"),sQuery(id+"F0.wireOp",EDGE,"E470"),sQuery(id+"F0.wireOp",EDGE,"E471"),sQuery(id+"F0.wireOp",EDGE,"E472"),sQuery(id+"F0.wireOp",EDGE,"E473"),sQuery(id+"F0.wireOp",EDGE,"E474"),sQuery(id+"F0.wireOp",EDGE,"E475"),sQuery(id+"F0.wireOp",EDGE,"E476"),sQuery(id+"F0.wireOp",EDGE,"E477"),sQuery(id+"F0.wireOp",EDGE,"E478"),sQuery(id+"F0.wireOp",EDGE,"E479"),sQuery(id+"F0.wireOp",EDGE,"E480"),sQuery(id+"F0.wireOp",EDGE,"E481"),sQuery(id+"F0.wireOp",EDGE,"E482"),sQuery(id+"F0.wireOp",EDGE,"E483"),sQuery(id+"F0.wireOp",EDGE,"E484"),sQuery(id+"F0.wireOp",EDGE,"E485"),sQuery(id+"F0.wireOp",EDGE,"E486"),sQuery(id+"F0.wireOp",EDGE,"E487"),sQuery(id+"F0.wireOp",EDGE,"E488"),sQuery(id+"F0.wireOp",EDGE,"E489"),sQuery(id+"F0.wireOp",EDGE,"E490"),sQuery(id+"F0.wireOp",EDGE,"E491"),sQuery(id+"F0.wireOp",EDGE,"E492"),sQuery(id+"F0.wireOp",EDGE,"E493"),sQuery(id+"F0.wireOp",EDGE,"E494"),sQuery(id+"F0.wireOp",EDGE,"E495"),sQuery(id+"F0.wireOp",EDGE,"E496"),sQuery(id+"F0.wireOp",EDGE,"E497"),sQuery(id+"F0.wireOp",EDGE,"E498"),sQuery(id+"F0.wireOp",EDGE,"E499"),sQuery(id+"F0.wireOp",EDGE,"E500"),sQuery(id+"F0.wireOp",EDGE,"E501"),sQuery(id+"F0.wireOp",EDGE,"E502"),sQuery(id+"F0.wireOp",EDGE,"E503"),sQuery(id+"F0.wireOp",EDGE,"E504"),sQuery(id+"F0.wireOp",EDGE,"E505"),sQuery(id+"F0.wireOp",EDGE,"E506"),sQuery(id+"F0.wireOp",EDGE,"E507"),sQuery(id+"F0.wireOp",EDGE,"E508"),sQuery(id+"F0.wireOp",EDGE,"E509"),sQuery(id+"F0.wireOp",EDGE,"E510"),sQuery(id+"F0.wireOp",EDGE,"E511"),sQuery(id+"F0.wireOp",EDGE,"E512"),sQuery(id+"F0.wireOp",EDGE,"E513"),sQuery(id+"F0.wireOp",EDGE,"E514"),sQuery(id+"F0.wireOp",EDGE,"E515"),sQuery(id+"F0.wireOp",EDGE,"E516"),sQuery(id+"F0.wireOp",EDGE,"E517"),sQuery(id+"F0.wireOp",EDGE,"E518"),sQuery(id+"F0.wireOp",EDGE,"E519"),sQuery(id+"F0.wireOp",EDGE,"E520"),sQuery(id+"F0.wireOp",EDGE,"E521"),sQuery(id+"F0.wireOp",EDGE,"E522"),sQuery(id+"F0.wireOp",EDGE,"E523"),sQuery(id+"F0.wireOp",EDGE,"E524"),sQuery(id+"F0.wireOp",EDGE,"E525"),sQuery(id+"F0.wireOp",EDGE,"E526"),sQuery(id+"F0.wireOp",EDGE,"E527"),sQuery(id+"F0.wireOp",EDGE,"E528"),sQuery(id+"F0.wireOp",EDGE,"E529"),sQuery(id+"F0.wireOp",EDGE,"E530"),sQuery(id+"F0.wireOp",EDGE,"E531"),sQuery(id+"F0.wireOp",EDGE,"E532"),sQuery(id+"F0.wireOp",EDGE,"E533"),sQuery(id+"F0.wireOp",EDGE,"E534"),sQuery(id+"F0.wireOp",EDGE,"E535"),sQuery(id+"F0.wireOp",EDGE,"E536"),sQuery(id+"F0.wireOp",EDGE,"E537"),sQuery(id+"F0.wireOp",EDGE,"E538"),sQuery(id+"F0.wireOp",EDGE,"E539")])],"isStart":false});
            var sketch = newSketch(context, id + "F2", { "sketchPlane" : qUnion([Q0])});
            skCircle(sketch, "E544.cCircle", {"center": v(0, 0) * mm, "radius": 3.15 * mm, "construction": true});
            skLineSegment(sketch, "E544.0", {"start": v(3.15, 1.82) * mm, "end": v(3.15, -1.82) * mm});
            skLineSegment(sketch, "E544.1", {"start": v(3.15, -1.82) * mm, "end": v(0, -3.64) * mm});
            skLineSegment(sketch, "E544.2", {"start": v(0, -3.64) * mm, "end": v(-3.15, -1.82) * mm});
            skLineSegment(sketch, "E544.3", {"start": v(-3.15, -1.82) * mm, "end": v(-3.15, 1.82) * mm});
            skLineSegment(sketch, "E544.4", {"start": v(-3.15, 1.82) * mm, "end": v(0, 3.64) * mm});
            skLineSegment(sketch, "E544.5", {"start": v(0, 3.64) * mm, "end": v(3.15, 1.82) * mm});
            skPoint(sketch, "E544.0.midPoint", {"position": v(3.15, 0) * mm});
            skSolve(sketch);
        }
        {
            var Q0;
            Q0=makeQuery(id+"F2.imprint","IMPRINT",FACE,{"disambiguationData":[TD([[makeQuery(id+"F2.imprint","IMPRINT",EDGE,{"derivedFrom":sQuery(id+"F2.wireOp",EDGE,"E544.0")}),-1.0]])]});
            extrude(context, id + "F3", {"entities" : qUnion([Q0]), "operationType" : NewBodyOperationType.REMOVE, "endBound" : BoundingType.THROUGH_ALL, "oppositeDirection" : true, "depth" : 25 * mm});
        }
        {
            var Q0;
            Q0=makeQuery(id+"F2.imprint","IMPRINT",FACE,{"disambiguationData":[TD([[makeQuery(id+"F2.imprint","IMPRINT",EDGE,{"derivedFrom":sQuery(id+"F2.wireOp",EDGE,"E544.0")}),1.0]])]});
            var sketch = newSketch(context, id + "F4", { "sketchPlane" : qUnion([Q0])});
            skCircle(sketch, "E545", {"center": v(0, 0) * mm, "radius": 12.75 * mm});
            skCircle(sketch, "E546", {"center": v(0, 0) * mm, "radius": 10.5 * mm});
            skLineSegment(sketch, "E547", {"start": v(0, 0) * mm, "end": v(-6.38, 11.04) * mm, "construction": true});
            skLineSegment(sketch, "E548", {"start": v(0, 0) * mm, "end": v(6.37, 11.04) * mm, "construction": true});
            skLineSegment(sketch, "E549", {"start": v(-6.38, 11.04) * mm, "end": v(-5.25, 9.1) * mm});
            skLineSegment(sketch, "E550", {"start": v(5.25, 9.1) * mm, "end": v(6.37, 11.04) * mm});
            skLineSegment(sketch, "E551", {"start": v(0, 0) * mm, "end": v(-12.75, 0) * mm, "construction": true});
            skLineSegment(sketch, "E552", {"start": v(0, 0) * mm, "end": v(-6.38, -11.04) * mm, "construction": true});
            skLineSegment(sketch, "E553", {"start": v(0, 0) * mm, "end": v(6.38, -11.04) * mm, "construction": true});
            skLineSegment(sketch, "E554", {"start": v(0, 0) * mm, "end": v(12.75, 0) * mm, "construction": true});
            skLineSegment(sketch, "E555", {"start": v(-10.5, 0) * mm, "end": v(-12.75, 0) * mm});
            skLineSegment(sketch, "E556", {"start": v(-5.25, -9.1) * mm, "end": v(-6.38, -11.04) * mm});
            skLineSegment(sketch, "E557", {"start": v(5.25, -9.1) * mm, "end": v(6.38, -11.04) * mm});
            skLineSegment(sketch, "E558", {"start": v(10.5, 0) * mm, "end": v(12.75, 0) * mm});
            skSolve(sketch);
        }
        {
            var Q0;
            {var subQ0=sQuery(id+"F4.wireOp",EDGE,"E549");Q0=makeQuery(id+"F4.imprint","IMPRINT",FACE,{"disambiguationData":[TD([[makeQuery(id+"F4.imprint","IMPRINT",EDGE,{"derivedFrom":subQ0}),1.0]])]});}
            var Q1;
            {var subQ0=sQuery(id+"F4.wireOp",EDGE,"E555");Q1=makeQuery(id+"F4.imprint","IMPRINT",FACE,{"disambiguationData":[TD([[makeQuery(id+"F4.imprint","IMPRINT",EDGE,{"derivedFrom":subQ0}),1.0]])]});}
            var Q2;
            {var subQ0=sQuery(id+"F4.wireOp",EDGE,"E557");Q2=makeQuery(id+"F4.imprint","IMPRINT",FACE,{"disambiguationData":[TD([[makeQuery(id+"F4.imprint","IMPRINT",EDGE,{"derivedFrom":subQ0}),1.0]])]});}
            extrude(context, id + "F5", {"entities" : qUnion([Q0, Q1, Q2]), "operationType" : NewBodyOperationType.REMOVE, "endBound" : BoundingType.THROUGH_ALL, "oppositeDirection" : true, "depth" : 25 * mm});
        }
    });
